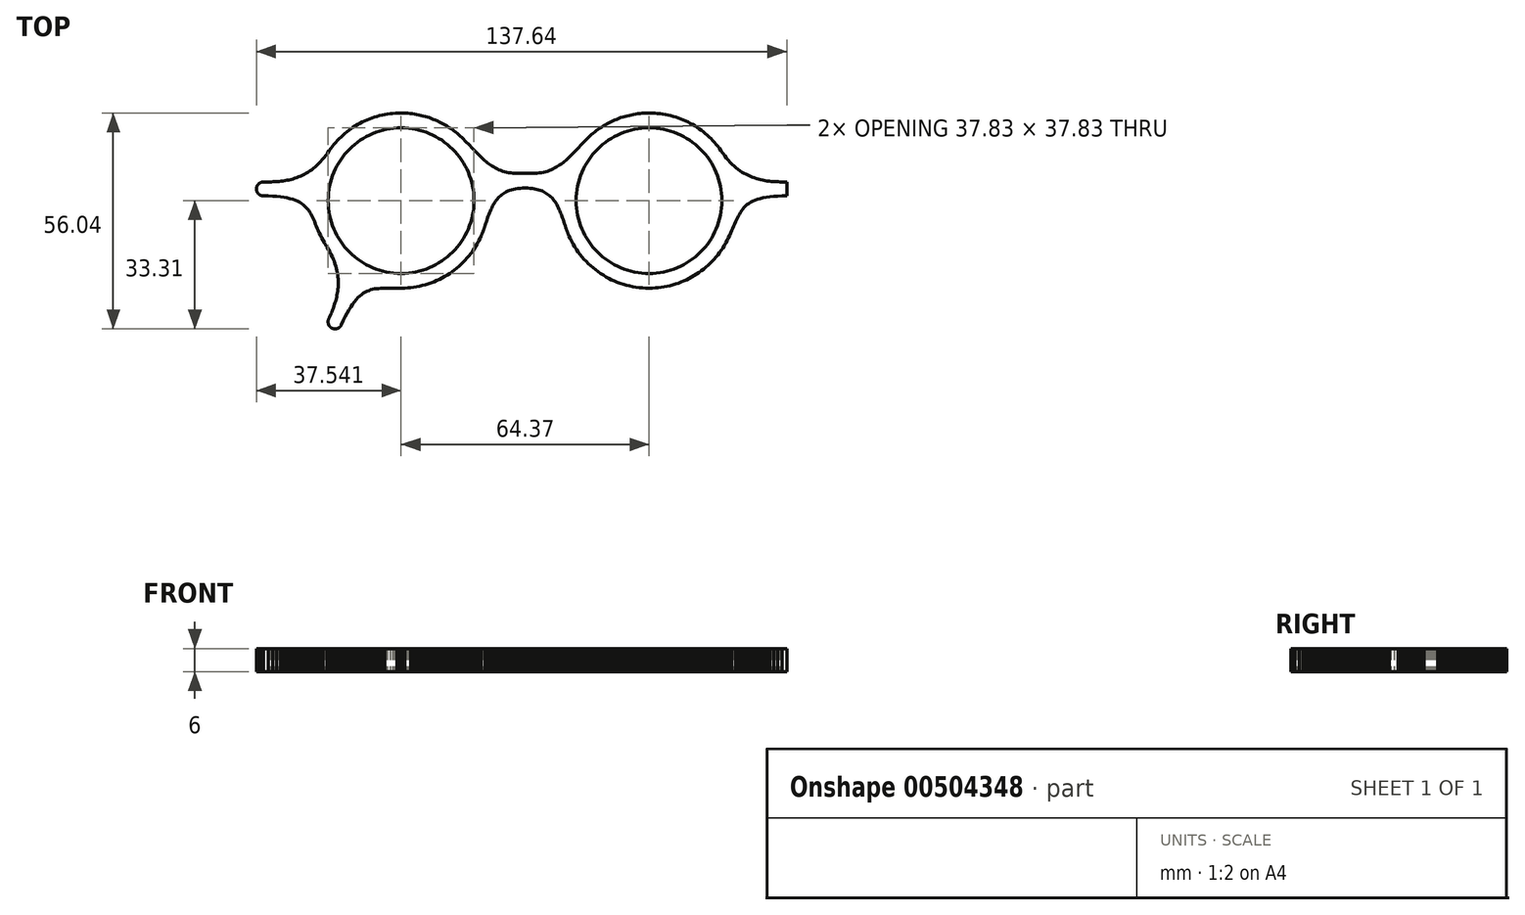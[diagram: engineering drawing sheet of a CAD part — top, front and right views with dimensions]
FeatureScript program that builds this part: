
annotation { "Feature Type Name" : "Feature", "Feature Type Description" : "" }
export const myFeature = defineFeature(function(context is Context, id is Id, definition is map)
    precondition{}
    {
        {
            var Q0;
            Q0=qCreatedBy(makeId("Top.planeOp"),FACE);
            var sketch = newSketch(context, id + "F0", { "sketchPlane" : qUnion([Q0])});
            skLineSegment(sketch, "E0", {"start": v(51.75, 18.26) * mm, "end": v(51.75, 18.26) * mm});
            skLineSegment(sketch, "E1", {"start": v(51.75, 18.26) * mm, "end": v(51.74, 18.27) * mm});
            skLineSegment(sketch, "E2", {"start": v(51.74, 18.27) * mm, "end": v(51.74, 18.27) * mm});
            skLineSegment(sketch, "E3", {"start": v(51.74, 18.27) * mm, "end": v(51.74, 18.28) * mm});
            skLineSegment(sketch, "E4", {"start": v(51.74, 18.28) * mm, "end": v(51.74, 18.28) * mm});
            skLineSegment(sketch, "E5", {"start": v(51.74, 18.28) * mm, "end": v(51.73, 18.28) * mm});
            skLineSegment(sketch, "E6", {"start": v(51.73, 18.28) * mm, "end": v(51.73, 18.28) * mm});
            skLineSegment(sketch, "E7", {"start": v(51.73, 18.28) * mm, "end": v(51.73, 18.29) * mm});
            skLineSegment(sketch, "E8", {"start": v(51.73, 18.29) * mm, "end": v(51.73, 18.29) * mm});
            skLineSegment(sketch, "E9", {"start": v(51.73, 18.29) * mm, "end": v(51.73, 18.28) * mm});
            skLineSegment(sketch, "E10", {"start": v(51.73, 18.28) * mm, "end": v(51.74, 18.28) * mm});
            skLineSegment(sketch, "E11", {"start": v(51.74, 18.28) * mm, "end": v(51.74, 18.27) * mm});
            skLineSegment(sketch, "E12", {"start": v(51.74, 18.27) * mm, "end": v(51.74, 18.26) * mm});
            skLineSegment(sketch, "E13", {"start": v(51.74, 18.26) * mm, "end": v(51.75, 18.26) * mm});
            skLineSegment(sketch, "E14", {"start": v(-49.93, 18.27) * mm, "end": v(-49.93, 18.27) * mm});
            skLineSegment(sketch, "E15", {"start": v(-49.93, 18.27) * mm, "end": v(-49.92, 18.28) * mm});
            skLineSegment(sketch, "E16", {"start": v(-49.92, 18.28) * mm, "end": v(-49.92, 18.28) * mm});
            skLineSegment(sketch, "E17", {"start": v(-49.92, 18.28) * mm, "end": v(-49.92, 18.29) * mm});
            skLineSegment(sketch, "E18", {"start": v(-49.92, 18.29) * mm, "end": v(-49.92, 18.29) * mm});
            skLineSegment(sketch, "E19", {"start": v(-49.92, 18.29) * mm, "end": v(-49.92, 18.28) * mm});
            skLineSegment(sketch, "E20", {"start": v(-49.92, 18.28) * mm, "end": v(-49.93, 18.27) * mm});
            skLineSegment(sketch, "E21", {"start": v(-49.93, 18.27) * mm, "end": v(-49.93, 18.26) * mm});
            skLineSegment(sketch, "E22", {"start": v(-49.93, 18.26) * mm, "end": v(-49.93, 18.26) * mm});
            skLineSegment(sketch, "E23", {"start": v(-49.93, 18.26) * mm, "end": v(-49.94, 18.26) * mm});
            skLineSegment(sketch, "E24", {"start": v(-49.94, 18.26) * mm, "end": v(-49.94, 18.26) * mm});
            skLineSegment(sketch, "E25", {"start": v(-49.94, 18.26) * mm, "end": v(-49.93, 18.26) * mm});
            skLineSegment(sketch, "E26", {"start": v(-49.93, 18.26) * mm, "end": v(-49.93, 18.27) * mm});
            skLineSegment(sketch, "E27", {"start": v(68.25, 10.13) * mm, "end": v(67.67, 10.14) * mm});
            skLineSegment(sketch, "E28", {"start": v(67.67, 10.14) * mm, "end": v(67.1, 10.15) * mm});
            skLineSegment(sketch, "E29", {"start": v(67.1, 10.15) * mm, "end": v(66.53, 10.17) * mm});
            skLineSegment(sketch, "E30", {"start": v(66.53, 10.17) * mm, "end": v(65.97, 10.2) * mm});
            skLineSegment(sketch, "E31", {"start": v(65.97, 10.2) * mm, "end": v(65.4, 10.23) * mm});
            skLineSegment(sketch, "E32", {"start": v(65.4, 10.23) * mm, "end": v(64.84, 10.28) * mm});
            skLineSegment(sketch, "E33", {"start": v(64.84, 10.28) * mm, "end": v(64.27, 10.34) * mm});
            skLineSegment(sketch, "E34", {"start": v(64.27, 10.34) * mm, "end": v(63.72, 10.41) * mm});
            skLineSegment(sketch, "E35", {"start": v(63.72, 10.41) * mm, "end": v(63.16, 10.5) * mm});
            skLineSegment(sketch, "E36", {"start": v(63.16, 10.5) * mm, "end": v(62.6, 10.6) * mm});
            skLineSegment(sketch, "E37", {"start": v(62.6, 10.6) * mm, "end": v(62.05, 10.72) * mm});
            skLineSegment(sketch, "E38", {"start": v(62.05, 10.72) * mm, "end": v(61.5, 10.85) * mm});
            skLineSegment(sketch, "E39", {"start": v(61.5, 10.85) * mm, "end": v(60.96, 11) * mm});
            skLineSegment(sketch, "E40", {"start": v(60.96, 11) * mm, "end": v(60.42, 11.18) * mm});
            skLineSegment(sketch, "E41", {"start": v(60.42, 11.18) * mm, "end": v(59.88, 11.38) * mm});
            skLineSegment(sketch, "E42", {"start": v(59.88, 11.38) * mm, "end": v(59.34, 11.6) * mm});
            skLineSegment(sketch, "E43", {"start": v(59.34, 11.6) * mm, "end": v(58.8, 11.83) * mm});
            skLineSegment(sketch, "E44", {"start": v(58.8, 11.83) * mm, "end": v(58.28, 12.1) * mm});
            skLineSegment(sketch, "E45", {"start": v(58.28, 12.1) * mm, "end": v(57.75, 12.38) * mm});
            skLineSegment(sketch, "E46", {"start": v(57.75, 12.38) * mm, "end": v(57.23, 12.7) * mm});
            skLineSegment(sketch, "E47", {"start": v(57.23, 12.7) * mm, "end": v(56.71, 13.04) * mm});
            skLineSegment(sketch, "E48", {"start": v(56.71, 13.04) * mm, "end": v(56.2, 13.42) * mm});
            skLineSegment(sketch, "E49", {"start": v(56.2, 13.42) * mm, "end": v(55.69, 13.82) * mm});
            skLineSegment(sketch, "E50", {"start": v(55.69, 13.82) * mm, "end": v(55.18, 14.25) * mm});
            skLineSegment(sketch, "E51", {"start": v(55.18, 14.25) * mm, "end": v(54.68, 14.72) * mm});
            skLineSegment(sketch, "E52", {"start": v(54.68, 14.72) * mm, "end": v(54.18, 15.22) * mm});
            skLineSegment(sketch, "E53", {"start": v(54.18, 15.22) * mm, "end": v(53.68, 15.75) * mm});
            skLineSegment(sketch, "E54", {"start": v(53.68, 15.75) * mm, "end": v(53.2, 16.32) * mm});
            skLineSegment(sketch, "E55", {"start": v(53.2, 16.32) * mm, "end": v(52.7, 16.93) * mm});
            skLineSegment(sketch, "E56", {"start": v(52.7, 16.93) * mm, "end": v(52.22, 17.57) * mm});
            skLineSegment(sketch, "E57", {"start": v(52.22, 17.57) * mm, "end": v(51.75, 18.26) * mm});
            skLineSegment(sketch, "E58", {"start": v(51.75, 18.26) * mm, "end": v(51.35, 18.8) * mm});
            skLineSegment(sketch, "E59", {"start": v(51.35, 18.8) * mm, "end": v(50.95, 19.34) * mm});
            skLineSegment(sketch, "E60", {"start": v(50.95, 19.34) * mm, "end": v(50.52, 19.86) * mm});
            skLineSegment(sketch, "E61", {"start": v(50.52, 19.86) * mm, "end": v(50.08, 20.37) * mm});
            skLineSegment(sketch, "E62", {"start": v(50.08, 20.37) * mm, "end": v(49.63, 20.87) * mm});
            skLineSegment(sketch, "E63", {"start": v(49.63, 20.87) * mm, "end": v(49.16, 21.35) * mm});
            skLineSegment(sketch, "E64", {"start": v(49.16, 21.35) * mm, "end": v(48.68, 21.82) * mm});
            skLineSegment(sketch, "E65", {"start": v(48.68, 21.82) * mm, "end": v(48.18, 22.27) * mm});
            skLineSegment(sketch, "E66", {"start": v(48.18, 22.27) * mm, "end": v(47.68, 22.71) * mm});
            skLineSegment(sketch, "E67", {"start": v(47.68, 22.71) * mm, "end": v(47.15, 23.14) * mm});
            skLineSegment(sketch, "E68", {"start": v(47.15, 23.14) * mm, "end": v(46.62, 23.55) * mm});
            skLineSegment(sketch, "E69", {"start": v(46.62, 23.55) * mm, "end": v(46.07, 23.94) * mm});
            skLineSegment(sketch, "E70", {"start": v(46.07, 23.94) * mm, "end": v(45.51, 24.32) * mm});
            skLineSegment(sketch, "E71", {"start": v(45.51, 24.32) * mm, "end": v(44.94, 24.68) * mm});
            skLineSegment(sketch, "E72", {"start": v(44.94, 24.68) * mm, "end": v(44.36, 25.02) * mm});
            skLineSegment(sketch, "E73", {"start": v(44.36, 25.02) * mm, "end": v(43.77, 25.35) * mm});
            skLineSegment(sketch, "E74", {"start": v(43.77, 25.35) * mm, "end": v(43.17, 25.66) * mm});
            skLineSegment(sketch, "E75", {"start": v(43.17, 25.66) * mm, "end": v(42.56, 25.96) * mm});
            skLineSegment(sketch, "E76", {"start": v(42.56, 25.96) * mm, "end": v(41.93, 26.23) * mm});
            skLineSegment(sketch, "E77", {"start": v(41.93, 26.23) * mm, "end": v(41.3, 26.49) * mm});
            skLineSegment(sketch, "E78", {"start": v(41.3, 26.49) * mm, "end": v(40.66, 26.73) * mm});
            skLineSegment(sketch, "E79", {"start": v(40.66, 26.73) * mm, "end": v(40.01, 26.95) * mm});
            skLineSegment(sketch, "E80", {"start": v(40.01, 26.95) * mm, "end": v(39.35, 27.15) * mm});
            skLineSegment(sketch, "E81", {"start": v(39.35, 27.15) * mm, "end": v(38.68, 27.33) * mm});
            skLineSegment(sketch, "E82", {"start": v(38.68, 27.33) * mm, "end": v(38, 27.49) * mm});
            skLineSegment(sketch, "E83", {"start": v(38, 27.49) * mm, "end": v(37.33, 27.63) * mm});
            skLineSegment(sketch, "E84", {"start": v(37.33, 27.63) * mm, "end": v(36.64, 27.75) * mm});
            skLineSegment(sketch, "E85", {"start": v(36.64, 27.75) * mm, "end": v(35.94, 27.85) * mm});
            skLineSegment(sketch, "E86", {"start": v(35.94, 27.85) * mm, "end": v(35.24, 27.92) * mm});
            skLineSegment(sketch, "E87", {"start": v(35.24, 27.92) * mm, "end": v(34.53, 27.98) * mm});
            skLineSegment(sketch, "E88", {"start": v(34.53, 27.98) * mm, "end": v(33.81, 28.01) * mm});
            skLineSegment(sketch, "E89", {"start": v(33.81, 28.01) * mm, "end": v(33.1, 28.02) * mm});
            skLineSegment(sketch, "E90", {"start": v(33.1, 28.02) * mm, "end": v(32.5, 28.02) * mm});
            skLineSegment(sketch, "E91", {"start": v(32.5, 28.02) * mm, "end": v(31.91, 28) * mm});
            skLineSegment(sketch, "E92", {"start": v(31.91, 28) * mm, "end": v(31.33, 27.96) * mm});
            skLineSegment(sketch, "E93", {"start": v(31.33, 27.96) * mm, "end": v(30.75, 27.9) * mm});
            skLineSegment(sketch, "E94", {"start": v(30.75, 27.9) * mm, "end": v(30.18, 27.84) * mm});
            skLineSegment(sketch, "E95", {"start": v(30.18, 27.84) * mm, "end": v(29.6, 27.76) * mm});
            skLineSegment(sketch, "E96", {"start": v(29.6, 27.76) * mm, "end": v(29.04, 27.66) * mm});
            skLineSegment(sketch, "E97", {"start": v(29.04, 27.66) * mm, "end": v(28.48, 27.55) * mm});
            skLineSegment(sketch, "E98", {"start": v(28.48, 27.55) * mm, "end": v(27.92, 27.43) * mm});
            skLineSegment(sketch, "E99", {"start": v(27.92, 27.43) * mm, "end": v(27.37, 27.3) * mm});
            skLineSegment(sketch, "E100", {"start": v(27.37, 27.3) * mm, "end": v(26.82, 27.14) * mm});
            skLineSegment(sketch, "E101", {"start": v(26.82, 27.14) * mm, "end": v(26.28, 26.98) * mm});
            skLineSegment(sketch, "E102", {"start": v(26.28, 26.98) * mm, "end": v(25.75, 26.8) * mm});
            skLineSegment(sketch, "E103", {"start": v(25.75, 26.8) * mm, "end": v(25.22, 26.62) * mm});
            skLineSegment(sketch, "E104", {"start": v(25.22, 26.62) * mm, "end": v(24.7, 26.42) * mm});
            skLineSegment(sketch, "E105", {"start": v(24.7, 26.42) * mm, "end": v(24.18, 26.2) * mm});
            skLineSegment(sketch, "E106", {"start": v(24.18, 26.2) * mm, "end": v(23.67, 25.98) * mm});
            skLineSegment(sketch, "E107", {"start": v(23.67, 25.98) * mm, "end": v(23.17, 25.74) * mm});
            skLineSegment(sketch, "E108", {"start": v(23.17, 25.74) * mm, "end": v(22.67, 25.5) * mm});
            skLineSegment(sketch, "E109", {"start": v(22.67, 25.5) * mm, "end": v(22.18, 25.23) * mm});
            skLineSegment(sketch, "E110", {"start": v(22.18, 25.23) * mm, "end": v(21.7, 24.96) * mm});
            skLineSegment(sketch, "E111", {"start": v(21.7, 24.96) * mm, "end": v(21.22, 24.67) * mm});
            skLineSegment(sketch, "E112", {"start": v(21.22, 24.67) * mm, "end": v(20.76, 24.38) * mm});
            skLineSegment(sketch, "E113", {"start": v(20.76, 24.38) * mm, "end": v(20.3, 24.07) * mm});
            skLineSegment(sketch, "E114", {"start": v(20.3, 24.07) * mm, "end": v(19.84, 23.75) * mm});
            skLineSegment(sketch, "E115", {"start": v(19.84, 23.75) * mm, "end": v(19.4, 23.43) * mm});
            skLineSegment(sketch, "E116", {"start": v(19.4, 23.43) * mm, "end": v(18.97, 23.09) * mm});
            skLineSegment(sketch, "E117", {"start": v(18.97, 23.09) * mm, "end": v(18.54, 22.74) * mm});
            skLineSegment(sketch, "E118", {"start": v(18.54, 22.74) * mm, "end": v(18.12, 22.38) * mm});
            skLineSegment(sketch, "E119", {"start": v(18.12, 22.38) * mm, "end": v(17.71, 22.01) * mm});
            skLineSegment(sketch, "E120", {"start": v(17.71, 22.01) * mm, "end": v(17.31, 21.64) * mm});
            skLineSegment(sketch, "E121", {"start": v(17.31, 21.64) * mm, "end": v(16.92, 21.25) * mm});
            skLineSegment(sketch, "E122", {"start": v(16.92, 21.25) * mm, "end": v(16.49, 20.82) * mm});
            skLineSegment(sketch, "E123", {"start": v(16.49, 20.82) * mm, "end": v(16.07, 20.4) * mm});
            skLineSegment(sketch, "E124", {"start": v(16.07, 20.4) * mm, "end": v(15.66, 19.98) * mm});
            skLineSegment(sketch, "E125", {"start": v(15.66, 19.98) * mm, "end": v(15.26, 19.56) * mm});
            skLineSegment(sketch, "E126", {"start": v(15.26, 19.56) * mm, "end": v(14.86, 19.15) * mm});
            skLineSegment(sketch, "E127", {"start": v(14.86, 19.15) * mm, "end": v(14.47, 18.74) * mm});
            skLineSegment(sketch, "E128", {"start": v(14.47, 18.74) * mm, "end": v(14.09, 18.34) * mm});
            skLineSegment(sketch, "E129", {"start": v(14.09, 18.34) * mm, "end": v(13.71, 17.95) * mm});
            skLineSegment(sketch, "E130", {"start": v(13.71, 17.95) * mm, "end": v(13.33, 17.56) * mm});
            skLineSegment(sketch, "E131", {"start": v(13.33, 17.56) * mm, "end": v(12.96, 17.18) * mm});
            skLineSegment(sketch, "E132", {"start": v(12.96, 17.18) * mm, "end": v(12.58, 16.8) * mm});
            skLineSegment(sketch, "E133", {"start": v(12.58, 16.8) * mm, "end": v(12.2, 16.44) * mm});
            skLineSegment(sketch, "E134", {"start": v(12.2, 16.44) * mm, "end": v(11.83, 16.1) * mm});
            skLineSegment(sketch, "E135", {"start": v(11.83, 16.1) * mm, "end": v(11.45, 15.75) * mm});
            skLineSegment(sketch, "E136", {"start": v(11.45, 15.75) * mm, "end": v(11.06, 15.42) * mm});
            skLineSegment(sketch, "E137", {"start": v(11.06, 15.42) * mm, "end": v(10.67, 15.1) * mm});
            skLineSegment(sketch, "E138", {"start": v(10.67, 15.1) * mm, "end": v(10.28, 14.8) * mm});
            skLineSegment(sketch, "E139", {"start": v(10.28, 14.8) * mm, "end": v(9.87, 14.5) * mm});
            skLineSegment(sketch, "E140", {"start": v(9.87, 14.5) * mm, "end": v(9.46, 14.23) * mm});
            skLineSegment(sketch, "E141", {"start": v(9.46, 14.23) * mm, "end": v(9.04, 13.98) * mm});
            skLineSegment(sketch, "E142", {"start": v(9.04, 13.98) * mm, "end": v(8.6, 13.73) * mm});
            skLineSegment(sketch, "E143", {"start": v(8.6, 13.73) * mm, "end": v(8.16, 13.5) * mm});
            skLineSegment(sketch, "E144", {"start": v(8.16, 13.5) * mm, "end": v(7.7, 13.3) * mm});
            skLineSegment(sketch, "E145", {"start": v(7.7, 13.3) * mm, "end": v(7.23, 13.1) * mm});
            skLineSegment(sketch, "E146", {"start": v(7.23, 13.1) * mm, "end": v(6.74, 12.94) * mm});
            skLineSegment(sketch, "E147", {"start": v(6.74, 12.94) * mm, "end": v(6.24, 12.79) * mm});
            skLineSegment(sketch, "E148", {"start": v(6.24, 12.79) * mm, "end": v(5.72, 12.66) * mm});
            skLineSegment(sketch, "E149", {"start": v(5.72, 12.66) * mm, "end": v(5.18, 12.55) * mm});
            skLineSegment(sketch, "E150", {"start": v(5.18, 12.55) * mm, "end": v(4.62, 12.47) * mm});
            skLineSegment(sketch, "E151", {"start": v(4.62, 12.47) * mm, "end": v(4.03, 12.4) * mm});
            skLineSegment(sketch, "E152", {"start": v(4.03, 12.4) * mm, "end": v(3.43, 12.37) * mm});
            skLineSegment(sketch, "E153", {"start": v(3.43, 12.37) * mm, "end": v(2.8, 12.36) * mm});
            skLineSegment(sketch, "E154", {"start": v(2.8, 12.36) * mm, "end": v(2.69, 12.36) * mm});
            skLineSegment(sketch, "E155", {"start": v(2.69, 12.36) * mm, "end": v(2.57, 12.36) * mm});
            skLineSegment(sketch, "E156", {"start": v(2.57, 12.36) * mm, "end": v(2.45, 12.36) * mm});
            skLineSegment(sketch, "E157", {"start": v(2.45, 12.36) * mm, "end": v(2.33, 12.36) * mm});
            skLineSegment(sketch, "E158", {"start": v(2.33, 12.36) * mm, "end": v(2.21, 12.36) * mm});
            skLineSegment(sketch, "E159", {"start": v(2.21, 12.36) * mm, "end": v(2.1, 12.36) * mm});
            skLineSegment(sketch, "E160", {"start": v(2.1, 12.36) * mm, "end": v(1.97, 12.36) * mm});
            skLineSegment(sketch, "E161", {"start": v(1.97, 12.36) * mm, "end": v(1.86, 12.36) * mm});
            skLineSegment(sketch, "E162", {"start": v(1.86, 12.36) * mm, "end": v(1.74, 12.36) * mm});
            skLineSegment(sketch, "E163", {"start": v(1.74, 12.36) * mm, "end": v(1.62, 12.36) * mm});
            skLineSegment(sketch, "E164", {"start": v(1.62, 12.36) * mm, "end": v(1.5, 12.36) * mm});
            skLineSegment(sketch, "E165", {"start": v(1.5, 12.36) * mm, "end": v(1.38, 12.36) * mm});
            skLineSegment(sketch, "E166", {"start": v(1.38, 12.36) * mm, "end": v(1.26, 12.36) * mm});
            skLineSegment(sketch, "E167", {"start": v(1.26, 12.36) * mm, "end": v(1.14, 12.36) * mm});
            skLineSegment(sketch, "E168", {"start": v(1.14, 12.36) * mm, "end": v(1.02, 12.36) * mm});
            skLineSegment(sketch, "E169", {"start": v(1.02, 12.36) * mm, "end": v(0.9, 12.36) * mm});
            skLineSegment(sketch, "E170", {"start": v(0.9, 12.36) * mm, "end": v(0.79, 12.36) * mm});
            skLineSegment(sketch, "E171", {"start": v(0.79, 12.36) * mm, "end": v(0.67, 12.36) * mm});
            skLineSegment(sketch, "E172", {"start": v(0.67, 12.36) * mm, "end": v(0.55, 12.36) * mm});
            skLineSegment(sketch, "E173", {"start": v(0.55, 12.36) * mm, "end": v(0.43, 12.36) * mm});
            skLineSegment(sketch, "E174", {"start": v(0.43, 12.36) * mm, "end": v(0.31, 12.36) * mm});
            skLineSegment(sketch, "E175", {"start": v(0.31, 12.36) * mm, "end": v(0.2, 12.36) * mm});
            skLineSegment(sketch, "E176", {"start": v(0.2, 12.36) * mm, "end": v(0.08, 12.36) * mm});
            skLineSegment(sketch, "E177", {"start": v(0.08, 12.36) * mm, "end": v(-0.04, 12.36) * mm});
            skLineSegment(sketch, "E178", {"start": v(-0.04, 12.36) * mm, "end": v(-0.16, 12.36) * mm});
            skLineSegment(sketch, "E179", {"start": v(-0.16, 12.36) * mm, "end": v(-0.28, 12.36) * mm});
            skLineSegment(sketch, "E180", {"start": v(-0.28, 12.36) * mm, "end": v(-0.4, 12.36) * mm});
            skLineSegment(sketch, "E181", {"start": v(-0.4, 12.36) * mm, "end": v(-0.52, 12.36) * mm});
            skLineSegment(sketch, "E182", {"start": v(-0.52, 12.36) * mm, "end": v(-0.64, 12.36) * mm});
            skLineSegment(sketch, "E183", {"start": v(-0.64, 12.36) * mm, "end": v(-0.75, 12.36) * mm});
            skLineSegment(sketch, "E184", {"start": v(-0.75, 12.36) * mm, "end": v(-0.87, 12.36) * mm});
            skLineSegment(sketch, "E185", {"start": v(-0.87, 12.36) * mm, "end": v(-1, 12.36) * mm});
            skLineSegment(sketch, "E186", {"start": v(-1, 12.36) * mm, "end": v(-1.62, 12.37) * mm});
            skLineSegment(sketch, "E187", {"start": v(-1.62, 12.37) * mm, "end": v(-2.22, 12.4) * mm});
            skLineSegment(sketch, "E188", {"start": v(-2.22, 12.4) * mm, "end": v(-2.8, 12.47) * mm});
            skLineSegment(sketch, "E189", {"start": v(-2.8, 12.47) * mm, "end": v(-3.36, 12.55) * mm});
            skLineSegment(sketch, "E190", {"start": v(-3.36, 12.55) * mm, "end": v(-3.9, 12.66) * mm});
            skLineSegment(sketch, "E191", {"start": v(-3.9, 12.66) * mm, "end": v(-4.43, 12.79) * mm});
            skLineSegment(sketch, "E192", {"start": v(-4.43, 12.79) * mm, "end": v(-4.93, 12.94) * mm});
            skLineSegment(sketch, "E193", {"start": v(-4.93, 12.94) * mm, "end": v(-5.42, 13.1) * mm});
            skLineSegment(sketch, "E194", {"start": v(-5.42, 13.1) * mm, "end": v(-5.9, 13.3) * mm});
            skLineSegment(sketch, "E195", {"start": v(-5.9, 13.3) * mm, "end": v(-6.35, 13.5) * mm});
            skLineSegment(sketch, "E196", {"start": v(-6.35, 13.5) * mm, "end": v(-6.8, 13.73) * mm});
            skLineSegment(sketch, "E197", {"start": v(-6.8, 13.73) * mm, "end": v(-7.23, 13.98) * mm});
            skLineSegment(sketch, "E198", {"start": v(-7.23, 13.98) * mm, "end": v(-7.65, 14.23) * mm});
            skLineSegment(sketch, "E199", {"start": v(-7.65, 14.23) * mm, "end": v(-8.06, 14.5) * mm});
            skLineSegment(sketch, "E200", {"start": v(-8.06, 14.5) * mm, "end": v(-8.46, 14.8) * mm});
            skLineSegment(sketch, "E201", {"start": v(-8.46, 14.8) * mm, "end": v(-8.86, 15.1) * mm});
            skLineSegment(sketch, "E202", {"start": v(-8.86, 15.1) * mm, "end": v(-9.25, 15.42) * mm});
            skLineSegment(sketch, "E203", {"start": v(-9.25, 15.42) * mm, "end": v(-9.64, 15.75) * mm});
            skLineSegment(sketch, "E204", {"start": v(-9.64, 15.75) * mm, "end": v(-10.02, 16.1) * mm});
            skLineSegment(sketch, "E205", {"start": v(-10.02, 16.1) * mm, "end": v(-10.4, 16.44) * mm});
            skLineSegment(sketch, "E206", {"start": v(-10.4, 16.44) * mm, "end": v(-10.77, 16.8) * mm});
            skLineSegment(sketch, "E207", {"start": v(-10.77, 16.8) * mm, "end": v(-11.15, 17.18) * mm});
            skLineSegment(sketch, "E208", {"start": v(-11.15, 17.18) * mm, "end": v(-11.52, 17.56) * mm});
            skLineSegment(sketch, "E209", {"start": v(-11.52, 17.56) * mm, "end": v(-11.9, 17.95) * mm});
            skLineSegment(sketch, "E210", {"start": v(-11.9, 17.95) * mm, "end": v(-12.28, 18.34) * mm});
            skLineSegment(sketch, "E211", {"start": v(-12.28, 18.34) * mm, "end": v(-12.66, 18.74) * mm});
            skLineSegment(sketch, "E212", {"start": v(-12.66, 18.74) * mm, "end": v(-13.05, 19.15) * mm});
            skLineSegment(sketch, "E213", {"start": v(-13.05, 19.15) * mm, "end": v(-13.45, 19.56) * mm});
            skLineSegment(sketch, "E214", {"start": v(-13.45, 19.56) * mm, "end": v(-13.85, 19.98) * mm});
            skLineSegment(sketch, "E215", {"start": v(-13.85, 19.98) * mm, "end": v(-14.26, 20.4) * mm});
            skLineSegment(sketch, "E216", {"start": v(-14.26, 20.4) * mm, "end": v(-14.68, 20.82) * mm});
            skLineSegment(sketch, "E217", {"start": v(-14.68, 20.82) * mm, "end": v(-15.1, 21.25) * mm});
            skLineSegment(sketch, "E218", {"start": v(-15.1, 21.25) * mm, "end": v(-15.5, 21.64) * mm});
            skLineSegment(sketch, "E219", {"start": v(-15.5, 21.64) * mm, "end": v(-15.9, 22.01) * mm});
            skLineSegment(sketch, "E220", {"start": v(-15.9, 22.01) * mm, "end": v(-16.3, 22.38) * mm});
            skLineSegment(sketch, "E221", {"start": v(-16.3, 22.38) * mm, "end": v(-16.73, 22.74) * mm});
            skLineSegment(sketch, "E222", {"start": v(-16.73, 22.74) * mm, "end": v(-17.15, 23.09) * mm});
            skLineSegment(sketch, "E223", {"start": v(-17.15, 23.09) * mm, "end": v(-17.59, 23.43) * mm});
            skLineSegment(sketch, "E224", {"start": v(-17.59, 23.43) * mm, "end": v(-18.03, 23.75) * mm});
            skLineSegment(sketch, "E225", {"start": v(-18.03, 23.75) * mm, "end": v(-18.48, 24.07) * mm});
            skLineSegment(sketch, "E226", {"start": v(-18.48, 24.07) * mm, "end": v(-18.94, 24.38) * mm});
            skLineSegment(sketch, "E227", {"start": v(-18.94, 24.38) * mm, "end": v(-19.41, 24.67) * mm});
            skLineSegment(sketch, "E228", {"start": v(-19.41, 24.67) * mm, "end": v(-19.89, 24.96) * mm});
            skLineSegment(sketch, "E229", {"start": v(-19.89, 24.96) * mm, "end": v(-20.37, 25.23) * mm});
            skLineSegment(sketch, "E230", {"start": v(-20.37, 25.23) * mm, "end": v(-20.86, 25.5) * mm});
            skLineSegment(sketch, "E231", {"start": v(-20.86, 25.5) * mm, "end": v(-21.36, 25.74) * mm});
            skLineSegment(sketch, "E232", {"start": v(-21.36, 25.74) * mm, "end": v(-21.86, 25.98) * mm});
            skLineSegment(sketch, "E233", {"start": v(-21.86, 25.98) * mm, "end": v(-22.37, 26.2) * mm});
            skLineSegment(sketch, "E234", {"start": v(-22.37, 26.2) * mm, "end": v(-22.89, 26.42) * mm});
            skLineSegment(sketch, "E235", {"start": v(-22.89, 26.42) * mm, "end": v(-23.4, 26.62) * mm});
            skLineSegment(sketch, "E236", {"start": v(-23.4, 26.62) * mm, "end": v(-23.94, 26.8) * mm});
            skLineSegment(sketch, "E237", {"start": v(-23.94, 26.8) * mm, "end": v(-24.47, 26.98) * mm});
            skLineSegment(sketch, "E238", {"start": v(-24.47, 26.98) * mm, "end": v(-25.01, 27.14) * mm});
            skLineSegment(sketch, "E239", {"start": v(-25.01, 27.14) * mm, "end": v(-25.56, 27.3) * mm});
            skLineSegment(sketch, "E240", {"start": v(-25.56, 27.3) * mm, "end": v(-26.1, 27.43) * mm});
            skLineSegment(sketch, "E241", {"start": v(-26.1, 27.43) * mm, "end": v(-26.67, 27.55) * mm});
            skLineSegment(sketch, "E242", {"start": v(-26.67, 27.55) * mm, "end": v(-27.23, 27.66) * mm});
            skLineSegment(sketch, "E243", {"start": v(-27.23, 27.66) * mm, "end": v(-27.8, 27.76) * mm});
            skLineSegment(sketch, "E244", {"start": v(-27.8, 27.76) * mm, "end": v(-28.36, 27.84) * mm});
            skLineSegment(sketch, "E245", {"start": v(-28.36, 27.84) * mm, "end": v(-28.94, 27.9) * mm});
            skLineSegment(sketch, "E246", {"start": v(-28.94, 27.9) * mm, "end": v(-29.52, 27.96) * mm});
            skLineSegment(sketch, "E247", {"start": v(-29.52, 27.96) * mm, "end": v(-30.1, 28) * mm});
            skLineSegment(sketch, "E248", {"start": v(-30.1, 28) * mm, "end": v(-30.69, 28.02) * mm});
            skLineSegment(sketch, "E249", {"start": v(-30.69, 28.02) * mm, "end": v(-31.28, 28.02) * mm});
            skLineSegment(sketch, "E250", {"start": v(-31.28, 28.02) * mm, "end": v(-32, 28.01) * mm});
            skLineSegment(sketch, "E251", {"start": v(-32, 28.01) * mm, "end": v(-32.72, 27.98) * mm});
            skLineSegment(sketch, "E252", {"start": v(-32.72, 27.98) * mm, "end": v(-33.42, 27.92) * mm});
            skLineSegment(sketch, "E253", {"start": v(-33.42, 27.92) * mm, "end": v(-34.13, 27.85) * mm});
            skLineSegment(sketch, "E254", {"start": v(-34.13, 27.85) * mm, "end": v(-34.82, 27.75) * mm});
            skLineSegment(sketch, "E255", {"start": v(-34.82, 27.75) * mm, "end": v(-35.51, 27.63) * mm});
            skLineSegment(sketch, "E256", {"start": v(-35.51, 27.63) * mm, "end": v(-36.2, 27.49) * mm});
            skLineSegment(sketch, "E257", {"start": v(-36.2, 27.49) * mm, "end": v(-36.87, 27.33) * mm});
            skLineSegment(sketch, "E258", {"start": v(-36.87, 27.33) * mm, "end": v(-37.54, 27.15) * mm});
            skLineSegment(sketch, "E259", {"start": v(-37.54, 27.15) * mm, "end": v(-38.2, 26.95) * mm});
            skLineSegment(sketch, "E260", {"start": v(-38.2, 26.95) * mm, "end": v(-38.85, 26.73) * mm});
            skLineSegment(sketch, "E261", {"start": v(-38.85, 26.73) * mm, "end": v(-39.49, 26.49) * mm});
            skLineSegment(sketch, "E262", {"start": v(-39.49, 26.49) * mm, "end": v(-40.12, 26.23) * mm});
            skLineSegment(sketch, "E263", {"start": v(-40.12, 26.23) * mm, "end": v(-40.74, 25.96) * mm});
            skLineSegment(sketch, "E264", {"start": v(-40.74, 25.96) * mm, "end": v(-41.36, 25.66) * mm});
            skLineSegment(sketch, "E265", {"start": v(-41.36, 25.66) * mm, "end": v(-41.96, 25.35) * mm});
            skLineSegment(sketch, "E266", {"start": v(-41.96, 25.35) * mm, "end": v(-42.55, 25.02) * mm});
            skLineSegment(sketch, "E267", {"start": v(-42.55, 25.02) * mm, "end": v(-43.13, 24.68) * mm});
            skLineSegment(sketch, "E268", {"start": v(-43.13, 24.68) * mm, "end": v(-43.7, 24.32) * mm});
            skLineSegment(sketch, "E269", {"start": v(-43.7, 24.32) * mm, "end": v(-44.26, 23.94) * mm});
            skLineSegment(sketch, "E270", {"start": v(-44.26, 23.94) * mm, "end": v(-44.8, 23.55) * mm});
            skLineSegment(sketch, "E271", {"start": v(-44.8, 23.55) * mm, "end": v(-45.34, 23.14) * mm});
            skLineSegment(sketch, "E272", {"start": v(-45.34, 23.14) * mm, "end": v(-45.86, 22.71) * mm});
            skLineSegment(sketch, "E273", {"start": v(-45.86, 22.71) * mm, "end": v(-46.37, 22.27) * mm});
            skLineSegment(sketch, "E274", {"start": v(-46.37, 22.27) * mm, "end": v(-46.87, 21.82) * mm});
            skLineSegment(sketch, "E275", {"start": v(-46.87, 21.82) * mm, "end": v(-47.35, 21.35) * mm});
            skLineSegment(sketch, "E276", {"start": v(-47.35, 21.35) * mm, "end": v(-47.82, 20.87) * mm});
            skLineSegment(sketch, "E277", {"start": v(-47.82, 20.87) * mm, "end": v(-48.27, 20.37) * mm});
            skLineSegment(sketch, "E278", {"start": v(-48.27, 20.37) * mm, "end": v(-48.7, 19.86) * mm});
            skLineSegment(sketch, "E279", {"start": v(-48.7, 19.86) * mm, "end": v(-49.13, 19.34) * mm});
            skLineSegment(sketch, "E280", {"start": v(-49.13, 19.34) * mm, "end": v(-49.54, 18.8) * mm});
            skLineSegment(sketch, "E281", {"start": v(-49.54, 18.8) * mm, "end": v(-49.94, 18.26) * mm});
            skLineSegment(sketch, "E282", {"start": v(-49.94, 18.26) * mm, "end": v(-50.37, 17.63) * mm});
            skLineSegment(sketch, "E283", {"start": v(-50.37, 17.63) * mm, "end": v(-50.81, 17.03) * mm});
            skLineSegment(sketch, "E284", {"start": v(-50.81, 17.03) * mm, "end": v(-51.26, 16.47) * mm});
            skLineSegment(sketch, "E285", {"start": v(-51.26, 16.47) * mm, "end": v(-51.7, 15.93) * mm});
            skLineSegment(sketch, "E286", {"start": v(-51.7, 15.93) * mm, "end": v(-52.16, 15.43) * mm});
            skLineSegment(sketch, "E287", {"start": v(-52.16, 15.43) * mm, "end": v(-52.62, 14.96) * mm});
            skLineSegment(sketch, "E288", {"start": v(-52.62, 14.96) * mm, "end": v(-53.08, 14.51) * mm});
            skLineSegment(sketch, "E289", {"start": v(-53.08, 14.51) * mm, "end": v(-53.54, 14.1) * mm});
            skLineSegment(sketch, "E290", {"start": v(-53.54, 14.1) * mm, "end": v(-54.01, 13.7) * mm});
            skLineSegment(sketch, "E291", {"start": v(-54.01, 13.7) * mm, "end": v(-54.48, 13.34) * mm});
            skLineSegment(sketch, "E292", {"start": v(-54.48, 13.34) * mm, "end": v(-54.96, 13) * mm});
            skLineSegment(sketch, "E293", {"start": v(-54.96, 13) * mm, "end": v(-55.44, 12.68) * mm});
            skLineSegment(sketch, "E294", {"start": v(-55.44, 12.68) * mm, "end": v(-55.92, 12.39) * mm});
            skLineSegment(sketch, "E295", {"start": v(-55.92, 12.39) * mm, "end": v(-56.4, 12.12) * mm});
            skLineSegment(sketch, "E296", {"start": v(-56.4, 12.12) * mm, "end": v(-56.89, 11.87) * mm});
            skLineSegment(sketch, "E297", {"start": v(-56.89, 11.87) * mm, "end": v(-57.37, 11.64) * mm});
            skLineSegment(sketch, "E298", {"start": v(-57.37, 11.64) * mm, "end": v(-57.87, 11.44) * mm});
            skLineSegment(sketch, "E299", {"start": v(-57.87, 11.44) * mm, "end": v(-58.36, 11.25) * mm});
            skLineSegment(sketch, "E300", {"start": v(-58.36, 11.25) * mm, "end": v(-58.86, 11.08) * mm});
            skLineSegment(sketch, "E301", {"start": v(-58.86, 11.08) * mm, "end": v(-59.36, 10.92) * mm});
            skLineSegment(sketch, "E302", {"start": v(-59.36, 10.92) * mm, "end": v(-59.86, 10.79) * mm});
            skLineSegment(sketch, "E303", {"start": v(-59.86, 10.79) * mm, "end": v(-60.36, 10.67) * mm});
            skLineSegment(sketch, "E304", {"start": v(-60.36, 10.67) * mm, "end": v(-60.87, 10.56) * mm});
            skLineSegment(sketch, "E305", {"start": v(-60.87, 10.56) * mm, "end": v(-61.38, 10.47) * mm});
            skLineSegment(sketch, "E306", {"start": v(-61.38, 10.47) * mm, "end": v(-61.89, 10.4) * mm});
            skLineSegment(sketch, "E307", {"start": v(-61.89, 10.4) * mm, "end": v(-62.4, 10.32) * mm});
            skLineSegment(sketch, "E308", {"start": v(-62.4, 10.32) * mm, "end": v(-62.91, 10.27) * mm});
            skLineSegment(sketch, "E309", {"start": v(-62.91, 10.27) * mm, "end": v(-63.43, 10.23) * mm});
            skLineSegment(sketch, "E310", {"start": v(-63.43, 10.23) * mm, "end": v(-63.94, 10.2) * mm});
            skLineSegment(sketch, "E311", {"start": v(-63.94, 10.2) * mm, "end": v(-64.46, 10.16) * mm});
            skLineSegment(sketch, "E312", {"start": v(-64.46, 10.16) * mm, "end": v(-64.98, 10.15) * mm});
            skLineSegment(sketch, "E313", {"start": v(-64.98, 10.15) * mm, "end": v(-65.5, 10.14) * mm});
            skLineSegment(sketch, "E314", {"start": v(-65.5, 10.14) * mm, "end": v(-65.55, 10.14) * mm});
            skLineSegment(sketch, "E315", {"start": v(-65.55, 10.14) * mm, "end": v(-65.6, 10.13) * mm});
            skLineSegment(sketch, "E316", {"start": v(-65.6, 10.13) * mm, "end": v(-65.64, 10.13) * mm});
            skLineSegment(sketch, "E317", {"start": v(-65.64, 10.13) * mm, "end": v(-65.69, 10.13) * mm});
            skLineSegment(sketch, "E318", {"start": v(-65.69, 10.13) * mm, "end": v(-65.74, 10.13) * mm});
            skLineSegment(sketch, "E319", {"start": v(-65.74, 10.13) * mm, "end": v(-65.78, 10.13) * mm});
            skLineSegment(sketch, "E320", {"start": v(-65.78, 10.13) * mm, "end": v(-65.83, 10.13) * mm});
            skLineSegment(sketch, "E321", {"start": v(-65.83, 10.13) * mm, "end": v(-65.88, 10.13) * mm});
            skLineSegment(sketch, "E322", {"start": v(-65.88, 10.13) * mm, "end": v(-65.93, 10.13) * mm});
            skLineSegment(sketch, "E323", {"start": v(-65.93, 10.13) * mm, "end": v(-65.97, 10.13) * mm});
            skLineSegment(sketch, "E324", {"start": v(-65.97, 10.13) * mm, "end": v(-66.02, 10.13) * mm});
            skLineSegment(sketch, "E325", {"start": v(-66.02, 10.13) * mm, "end": v(-66.07, 10.13) * mm});
            skLineSegment(sketch, "E326", {"start": v(-66.07, 10.13) * mm, "end": v(-66.11, 10.13) * mm});
            skLineSegment(sketch, "E327", {"start": v(-66.11, 10.13) * mm, "end": v(-66.16, 10.13) * mm});
            skLineSegment(sketch, "E328", {"start": v(-66.16, 10.13) * mm, "end": v(-66.2, 10.13) * mm});
            skLineSegment(sketch, "E329", {"start": v(-66.2, 10.13) * mm, "end": v(-66.26, 10.13) * mm});
            skLineSegment(sketch, "E330", {"start": v(-66.26, 10.13) * mm, "end": v(-66.3, 10.13) * mm});
            skLineSegment(sketch, "E331", {"start": v(-66.3, 10.13) * mm, "end": v(-66.35, 10.13) * mm});
            skLineSegment(sketch, "E332", {"start": v(-66.35, 10.13) * mm, "end": v(-66.4, 10.13) * mm});
            skLineSegment(sketch, "E333", {"start": v(-66.4, 10.13) * mm, "end": v(-66.44, 10.13) * mm});
            skLineSegment(sketch, "E334", {"start": v(-66.44, 10.13) * mm, "end": v(-66.5, 10.13) * mm});
            skLineSegment(sketch, "E335", {"start": v(-66.5, 10.13) * mm, "end": v(-66.54, 10.13) * mm});
            skLineSegment(sketch, "E336", {"start": v(-66.54, 10.13) * mm, "end": v(-66.59, 10.13) * mm});
            skLineSegment(sketch, "E337", {"start": v(-66.59, 10.13) * mm, "end": v(-66.63, 10.13) * mm});
            skLineSegment(sketch, "E338", {"start": v(-66.63, 10.13) * mm, "end": v(-66.68, 10.13) * mm});
            skLineSegment(sketch, "E339", {"start": v(-66.68, 10.13) * mm, "end": v(-66.73, 10.13) * mm});
            skLineSegment(sketch, "E340", {"start": v(-66.73, 10.13) * mm, "end": v(-66.78, 10.13) * mm});
            skLineSegment(sketch, "E341", {"start": v(-66.78, 10.13) * mm, "end": v(-66.82, 10.13) * mm});
            skLineSegment(sketch, "E342", {"start": v(-66.82, 10.13) * mm, "end": v(-66.87, 10.13) * mm});
            skLineSegment(sketch, "E343", {"start": v(-66.87, 10.13) * mm, "end": v(-66.92, 10.13) * mm});
            skLineSegment(sketch, "E344", {"start": v(-66.92, 10.13) * mm, "end": v(-66.96, 10.13) * mm});
            skLineSegment(sketch, "E345", {"start": v(-66.96, 10.13) * mm, "end": v(-67.01, 10.13) * mm});
            skLineSegment(sketch, "E346", {"start": v(-67.01, 10.13) * mm, "end": v(-67.01, 10.13) * mm});
            skLineSegment(sketch, "E347", {"start": v(-67.01, 10.13) * mm, "end": v(-67.1, 10.12) * mm});
            skLineSegment(sketch, "E348", {"start": v(-67.1, 10.12) * mm, "end": v(-67.2, 10.12) * mm});
            skLineSegment(sketch, "E349", {"start": v(-67.2, 10.12) * mm, "end": v(-67.29, 10.1) * mm});
            skLineSegment(sketch, "E350", {"start": v(-67.29, 10.1) * mm, "end": v(-67.38, 10.09) * mm});
            skLineSegment(sketch, "E351", {"start": v(-67.38, 10.09) * mm, "end": v(-67.46, 10.07) * mm});
            skLineSegment(sketch, "E352", {"start": v(-67.46, 10.07) * mm, "end": v(-67.55, 10.04) * mm});
            skLineSegment(sketch, "E353", {"start": v(-67.55, 10.04) * mm, "end": v(-67.63, 10.02) * mm});
            skLineSegment(sketch, "E354", {"start": v(-67.63, 10.02) * mm, "end": v(-67.72, 9.98) * mm});
            skLineSegment(sketch, "E355", {"start": v(-67.72, 9.98) * mm, "end": v(-67.8, 9.95) * mm});
            skLineSegment(sketch, "E356", {"start": v(-67.8, 9.95) * mm, "end": v(-67.87, 9.9) * mm});
            skLineSegment(sketch, "E357", {"start": v(-67.87, 9.9) * mm, "end": v(-67.95, 9.86) * mm});
            skLineSegment(sketch, "E358", {"start": v(-67.95, 9.86) * mm, "end": v(-68.02, 9.82) * mm});
            skLineSegment(sketch, "E359", {"start": v(-68.02, 9.82) * mm, "end": v(-68.1, 9.77) * mm});
            skLineSegment(sketch, "E360", {"start": v(-68.1, 9.77) * mm, "end": v(-68.16, 9.71) * mm});
            skLineSegment(sketch, "E361", {"start": v(-68.16, 9.71) * mm, "end": v(-68.23, 9.65) * mm});
            skLineSegment(sketch, "E362", {"start": v(-68.23, 9.65) * mm, "end": v(-68.3, 9.6) * mm});
            skLineSegment(sketch, "E363", {"start": v(-68.3, 9.6) * mm, "end": v(-68.35, 9.53) * mm});
            skLineSegment(sketch, "E364", {"start": v(-68.35, 9.53) * mm, "end": v(-68.4, 9.47) * mm});
            skLineSegment(sketch, "E365", {"start": v(-68.4, 9.47) * mm, "end": v(-68.46, 9.4) * mm});
            skLineSegment(sketch, "E366", {"start": v(-68.46, 9.4) * mm, "end": v(-68.51, 9.33) * mm});
            skLineSegment(sketch, "E367", {"start": v(-68.51, 9.33) * mm, "end": v(-68.56, 9.25) * mm});
            skLineSegment(sketch, "E368", {"start": v(-68.56, 9.25) * mm, "end": v(-68.6, 9.18) * mm});
            skLineSegment(sketch, "E369", {"start": v(-68.6, 9.18) * mm, "end": v(-68.64, 9.1) * mm});
            skLineSegment(sketch, "E370", {"start": v(-68.64, 9.1) * mm, "end": v(-68.68, 9.02) * mm});
            skLineSegment(sketch, "E371", {"start": v(-68.68, 9.02) * mm, "end": v(-68.71, 8.94) * mm});
            skLineSegment(sketch, "E372", {"start": v(-68.71, 8.94) * mm, "end": v(-68.74, 8.85) * mm});
            skLineSegment(sketch, "E373", {"start": v(-68.74, 8.85) * mm, "end": v(-68.77, 8.77) * mm});
            skLineSegment(sketch, "E374", {"start": v(-68.77, 8.77) * mm, "end": v(-68.79, 8.68) * mm});
            skLineSegment(sketch, "E375", {"start": v(-68.79, 8.68) * mm, "end": v(-68.8, 8.59) * mm});
            skLineSegment(sketch, "E376", {"start": v(-68.8, 8.59) * mm, "end": v(-68.81, 8.5) * mm});
            skLineSegment(sketch, "E377", {"start": v(-68.81, 8.5) * mm, "end": v(-68.82, 8.4) * mm});
            skLineSegment(sketch, "E378", {"start": v(-68.82, 8.4) * mm, "end": v(-68.82, 8.31) * mm});
            skLineSegment(sketch, "E379", {"start": v(-68.82, 8.31) * mm, "end": v(-68.82, 8.22) * mm});
            skLineSegment(sketch, "E380", {"start": v(-68.82, 8.22) * mm, "end": v(-68.81, 8.13) * mm});
            skLineSegment(sketch, "E381", {"start": v(-68.81, 8.13) * mm, "end": v(-68.8, 8.04) * mm});
            skLineSegment(sketch, "E382", {"start": v(-68.8, 8.04) * mm, "end": v(-68.79, 7.95) * mm});
            skLineSegment(sketch, "E383", {"start": v(-68.79, 7.95) * mm, "end": v(-68.77, 7.86) * mm});
            skLineSegment(sketch, "E384", {"start": v(-68.77, 7.86) * mm, "end": v(-68.74, 7.77) * mm});
            skLineSegment(sketch, "E385", {"start": v(-68.74, 7.77) * mm, "end": v(-68.71, 7.7) * mm});
            skLineSegment(sketch, "E386", {"start": v(-68.71, 7.7) * mm, "end": v(-68.68, 7.6) * mm});
            skLineSegment(sketch, "E387", {"start": v(-68.68, 7.6) * mm, "end": v(-68.64, 7.53) * mm});
            skLineSegment(sketch, "E388", {"start": v(-68.64, 7.53) * mm, "end": v(-68.6, 7.45) * mm});
            skLineSegment(sketch, "E389", {"start": v(-68.6, 7.45) * mm, "end": v(-68.56, 7.37) * mm});
            skLineSegment(sketch, "E390", {"start": v(-68.56, 7.37) * mm, "end": v(-68.51, 7.3) * mm});
            skLineSegment(sketch, "E391", {"start": v(-68.51, 7.3) * mm, "end": v(-68.46, 7.23) * mm});
            skLineSegment(sketch, "E392", {"start": v(-68.46, 7.23) * mm, "end": v(-68.4, 7.16) * mm});
            skLineSegment(sketch, "E393", {"start": v(-68.4, 7.16) * mm, "end": v(-68.35, 7.1) * mm});
            skLineSegment(sketch, "E394", {"start": v(-68.35, 7.1) * mm, "end": v(-68.3, 7.03) * mm});
            skLineSegment(sketch, "E395", {"start": v(-68.3, 7.03) * mm, "end": v(-68.23, 6.97) * mm});
            skLineSegment(sketch, "E396", {"start": v(-68.23, 6.97) * mm, "end": v(-68.16, 6.91) * mm});
            skLineSegment(sketch, "E397", {"start": v(-68.16, 6.91) * mm, "end": v(-68.1, 6.86) * mm});
            skLineSegment(sketch, "E398", {"start": v(-68.1, 6.86) * mm, "end": v(-68.02, 6.81) * mm});
            skLineSegment(sketch, "E399", {"start": v(-68.02, 6.81) * mm, "end": v(-67.95, 6.76) * mm});
            skLineSegment(sketch, "E400", {"start": v(-67.95, 6.76) * mm, "end": v(-67.87, 6.72) * mm});
            skLineSegment(sketch, "E401", {"start": v(-67.87, 6.72) * mm, "end": v(-67.8, 6.68) * mm});
            skLineSegment(sketch, "E402", {"start": v(-67.8, 6.68) * mm, "end": v(-67.72, 6.64) * mm});
            skLineSegment(sketch, "E403", {"start": v(-67.72, 6.64) * mm, "end": v(-67.63, 6.61) * mm});
            skLineSegment(sketch, "E404", {"start": v(-67.63, 6.61) * mm, "end": v(-67.55, 6.58) * mm});
            skLineSegment(sketch, "E405", {"start": v(-67.55, 6.58) * mm, "end": v(-67.46, 6.56) * mm});
            skLineSegment(sketch, "E406", {"start": v(-67.46, 6.56) * mm, "end": v(-67.38, 6.54) * mm});
            skLineSegment(sketch, "E407", {"start": v(-67.38, 6.54) * mm, "end": v(-67.29, 6.52) * mm});
            skLineSegment(sketch, "E408", {"start": v(-67.29, 6.52) * mm, "end": v(-67.2, 6.51) * mm});
            skLineSegment(sketch, "E409", {"start": v(-67.2, 6.51) * mm, "end": v(-67.1, 6.5) * mm});
            skLineSegment(sketch, "E410", {"start": v(-67.1, 6.5) * mm, "end": v(-67.01, 6.5) * mm});
            skLineSegment(sketch, "E411", {"start": v(-67.01, 6.5) * mm, "end": v(-67.01, 6.5) * mm});
            skLineSegment(sketch, "E412", {"start": v(-67.01, 6.5) * mm, "end": v(-65.79, 6.49) * mm});
            skLineSegment(sketch, "E413", {"start": v(-65.79, 6.49) * mm, "end": v(-64.65, 6.44) * mm});
            skLineSegment(sketch, "E414", {"start": v(-64.65, 6.44) * mm, "end": v(-63.6, 6.37) * mm});
            skLineSegment(sketch, "E415", {"start": v(-63.6, 6.37) * mm, "end": v(-62.62, 6.27) * mm});
            skLineSegment(sketch, "E416", {"start": v(-62.62, 6.27) * mm, "end": v(-61.71, 6.14) * mm});
            skLineSegment(sketch, "E417", {"start": v(-61.71, 6.14) * mm, "end": v(-60.88, 5.99) * mm});
            skLineSegment(sketch, "E418", {"start": v(-60.88, 5.99) * mm, "end": v(-60.12, 5.8) * mm});
            skLineSegment(sketch, "E419", {"start": v(-60.12, 5.8) * mm, "end": v(-59.41, 5.6) * mm});
            skLineSegment(sketch, "E420", {"start": v(-59.41, 5.6) * mm, "end": v(-58.77, 5.37) * mm});
            skLineSegment(sketch, "E421", {"start": v(-58.77, 5.37) * mm, "end": v(-58.18, 5.11) * mm});
            skLineSegment(sketch, "E422", {"start": v(-58.18, 5.11) * mm, "end": v(-57.64, 4.83) * mm});
            skLineSegment(sketch, "E423", {"start": v(-57.64, 4.83) * mm, "end": v(-57.15, 4.53) * mm});
            skLineSegment(sketch, "E424", {"start": v(-57.15, 4.53) * mm, "end": v(-56.7, 4.2) * mm});
            skLineSegment(sketch, "E425", {"start": v(-56.7, 4.2) * mm, "end": v(-56.3, 3.85) * mm});
            skLineSegment(sketch, "E426", {"start": v(-56.3, 3.85) * mm, "end": v(-55.92, 3.48) * mm});
            skLineSegment(sketch, "E427", {"start": v(-55.92, 3.48) * mm, "end": v(-55.57, 3.09) * mm});
            skLineSegment(sketch, "E428", {"start": v(-55.57, 3.09) * mm, "end": v(-55.26, 2.67) * mm});
            skLineSegment(sketch, "E429", {"start": v(-55.26, 2.67) * mm, "end": v(-54.97, 2.24) * mm});
            skLineSegment(sketch, "E430", {"start": v(-54.97, 2.24) * mm, "end": v(-54.7, 1.78) * mm});
            skLineSegment(sketch, "E431", {"start": v(-54.7, 1.78) * mm, "end": v(-54.44, 1.31) * mm});
            skLineSegment(sketch, "E432", {"start": v(-54.44, 1.31) * mm, "end": v(-54.2, 0.82) * mm});
            skLineSegment(sketch, "E433", {"start": v(-54.2, 0.82) * mm, "end": v(-53.96, 0.3) * mm});
            skLineSegment(sketch, "E434", {"start": v(-53.96, 0.3) * mm, "end": v(-53.73, -0.22) * mm});
            skLineSegment(sketch, "E435", {"start": v(-53.73, -0.22) * mm, "end": v(-53.5, -0.77) * mm});
            skLineSegment(sketch, "E436", {"start": v(-53.5, -0.77) * mm, "end": v(-53.26, -1.33) * mm});
            skLineSegment(sketch, "E437", {"start": v(-53.26, -1.33) * mm, "end": v(-53.01, -1.91) * mm});
            skLineSegment(sketch, "E438", {"start": v(-53.01, -1.91) * mm, "end": v(-52.76, -2.5) * mm});
            skLineSegment(sketch, "E439", {"start": v(-52.76, -2.5) * mm, "end": v(-52.49, -3.11) * mm});
            skLineSegment(sketch, "E440", {"start": v(-52.49, -3.11) * mm, "end": v(-52.2, -3.74) * mm});
            skLineSegment(sketch, "E441", {"start": v(-52.2, -3.74) * mm, "end": v(-51.89, -4.38) * mm});
            skLineSegment(sketch, "E442", {"start": v(-51.89, -4.38) * mm, "end": v(-51.55, -5.03) * mm});
            skLineSegment(sketch, "E443", {"start": v(-51.55, -5.03) * mm, "end": v(-51.17, -5.7) * mm});
            skLineSegment(sketch, "E444", {"start": v(-51.17, -5.7) * mm, "end": v(-51.15, -5.73) * mm});
            skLineSegment(sketch, "E445", {"start": v(-51.15, -5.73) * mm, "end": v(-51.14, -5.77) * mm});
            skLineSegment(sketch, "E446", {"start": v(-51.14, -5.77) * mm, "end": v(-51.12, -5.8) * mm});
            skLineSegment(sketch, "E447", {"start": v(-51.12, -5.8) * mm, "end": v(-51.1, -5.84) * mm});
            skLineSegment(sketch, "E448", {"start": v(-51.1, -5.84) * mm, "end": v(-51.08, -5.87) * mm});
            skLineSegment(sketch, "E449", {"start": v(-51.08, -5.87) * mm, "end": v(-51.06, -5.9) * mm});
            skLineSegment(sketch, "E450", {"start": v(-51.06, -5.9) * mm, "end": v(-51.04, -5.94) * mm});
            skLineSegment(sketch, "E451", {"start": v(-51.04, -5.94) * mm, "end": v(-51.02, -5.98) * mm});
            skLineSegment(sketch, "E452", {"start": v(-51.02, -5.98) * mm, "end": v(-51, -6.01) * mm});
            skLineSegment(sketch, "E453", {"start": v(-51, -6.01) * mm, "end": v(-50.98, -6.04) * mm});
            skLineSegment(sketch, "E454", {"start": v(-50.98, -6.04) * mm, "end": v(-50.96, -6.08) * mm});
            skLineSegment(sketch, "E455", {"start": v(-50.96, -6.08) * mm, "end": v(-50.94, -6.11) * mm});
            skLineSegment(sketch, "E456", {"start": v(-50.94, -6.11) * mm, "end": v(-50.91, -6.15) * mm});
            skLineSegment(sketch, "E457", {"start": v(-50.91, -6.15) * mm, "end": v(-50.9, -6.18) * mm});
            skLineSegment(sketch, "E458", {"start": v(-50.9, -6.18) * mm, "end": v(-50.87, -6.22) * mm});
            skLineSegment(sketch, "E459", {"start": v(-50.87, -6.22) * mm, "end": v(-50.85, -6.25) * mm});
            skLineSegment(sketch, "E460", {"start": v(-50.85, -6.25) * mm, "end": v(-50.83, -6.29) * mm});
            skLineSegment(sketch, "E461", {"start": v(-50.83, -6.29) * mm, "end": v(-50.81, -6.32) * mm});
            skLineSegment(sketch, "E462", {"start": v(-50.81, -6.32) * mm, "end": v(-50.8, -6.36) * mm});
            skLineSegment(sketch, "E463", {"start": v(-50.8, -6.36) * mm, "end": v(-50.77, -6.4) * mm});
            skLineSegment(sketch, "E464", {"start": v(-50.77, -6.4) * mm, "end": v(-50.75, -6.42) * mm});
            skLineSegment(sketch, "E465", {"start": v(-50.75, -6.42) * mm, "end": v(-50.73, -6.46) * mm});
            skLineSegment(sketch, "E466", {"start": v(-50.73, -6.46) * mm, "end": v(-50.7, -6.5) * mm});
            skLineSegment(sketch, "E467", {"start": v(-50.7, -6.5) * mm, "end": v(-50.69, -6.53) * mm});
            skLineSegment(sketch, "E468", {"start": v(-50.69, -6.53) * mm, "end": v(-50.67, -6.56) * mm});
            skLineSegment(sketch, "E469", {"start": v(-50.67, -6.56) * mm, "end": v(-50.65, -6.6) * mm});
            skLineSegment(sketch, "E470", {"start": v(-50.65, -6.6) * mm, "end": v(-50.62, -6.63) * mm});
            skLineSegment(sketch, "E471", {"start": v(-50.62, -6.63) * mm, "end": v(-50.6, -6.66) * mm});
            skLineSegment(sketch, "E472", {"start": v(-50.6, -6.66) * mm, "end": v(-50.58, -6.7) * mm});
            skLineSegment(sketch, "E473", {"start": v(-50.58, -6.7) * mm, "end": v(-50.56, -6.73) * mm});
            skLineSegment(sketch, "E474", {"start": v(-50.56, -6.73) * mm, "end": v(-50.54, -6.77) * mm});
            skLineSegment(sketch, "E475", {"start": v(-50.54, -6.77) * mm, "end": v(-50.52, -6.8) * mm});
            skLineSegment(sketch, "E476", {"start": v(-50.52, -6.8) * mm, "end": v(-50.13, -7.44) * mm});
            skLineSegment(sketch, "E477", {"start": v(-50.13, -7.44) * mm, "end": v(-49.78, -8.08) * mm});
            skLineSegment(sketch, "E478", {"start": v(-49.78, -8.08) * mm, "end": v(-49.45, -8.7) * mm});
            skLineSegment(sketch, "E479", {"start": v(-49.45, -8.7) * mm, "end": v(-49.16, -9.32) * mm});
            skLineSegment(sketch, "E480", {"start": v(-49.16, -9.32) * mm, "end": v(-48.89, -9.93) * mm});
            skLineSegment(sketch, "E481", {"start": v(-48.89, -9.93) * mm, "end": v(-48.65, -10.53) * mm});
            skLineSegment(sketch, "E482", {"start": v(-48.65, -10.53) * mm, "end": v(-48.44, -11.12) * mm});
            skLineSegment(sketch, "E483", {"start": v(-48.44, -11.12) * mm, "end": v(-48.25, -11.7) * mm});
            skLineSegment(sketch, "E484", {"start": v(-48.25, -11.7) * mm, "end": v(-48.09, -12.28) * mm});
            skLineSegment(sketch, "E485", {"start": v(-48.09, -12.28) * mm, "end": v(-47.95, -12.85) * mm});
            skLineSegment(sketch, "E486", {"start": v(-47.95, -12.85) * mm, "end": v(-47.83, -13.42) * mm});
            skLineSegment(sketch, "E487", {"start": v(-47.83, -13.42) * mm, "end": v(-47.74, -13.97) * mm});
            skLineSegment(sketch, "E488", {"start": v(-47.74, -13.97) * mm, "end": v(-47.67, -14.52) * mm});
            skLineSegment(sketch, "E489", {"start": v(-47.67, -14.52) * mm, "end": v(-47.62, -15.07) * mm});
            skLineSegment(sketch, "E490", {"start": v(-47.62, -15.07) * mm, "end": v(-47.6, -15.6) * mm});
            skLineSegment(sketch, "E491", {"start": v(-47.6, -15.6) * mm, "end": v(-47.59, -16.14) * mm});
            skLineSegment(sketch, "E492", {"start": v(-47.59, -16.14) * mm, "end": v(-47.6, -16.67) * mm});
            skLineSegment(sketch, "E493", {"start": v(-47.6, -16.67) * mm, "end": v(-47.63, -17.19) * mm});
            skLineSegment(sketch, "E494", {"start": v(-47.63, -17.19) * mm, "end": v(-47.67, -17.7) * mm});
            skLineSegment(sketch, "E495", {"start": v(-47.67, -17.7) * mm, "end": v(-47.74, -18.22) * mm});
            skLineSegment(sketch, "E496", {"start": v(-47.74, -18.22) * mm, "end": v(-47.81, -18.73) * mm});
            skLineSegment(sketch, "E497", {"start": v(-47.81, -18.73) * mm, "end": v(-47.9, -19.23) * mm});
            skLineSegment(sketch, "E498", {"start": v(-47.9, -19.23) * mm, "end": v(-48.01, -19.73) * mm});
            skLineSegment(sketch, "E499", {"start": v(-48.01, -19.73) * mm, "end": v(-48.13, -20.23) * mm});
            skLineSegment(sketch, "E500", {"start": v(-48.13, -20.23) * mm, "end": v(-48.27, -20.72) * mm});
            skLineSegment(sketch, "E501", {"start": v(-48.27, -20.72) * mm, "end": v(-48.4, -21.21) * mm});
            skLineSegment(sketch, "E502", {"start": v(-48.4, -21.21) * mm, "end": v(-48.56, -21.7) * mm});
            skLineSegment(sketch, "E503", {"start": v(-48.56, -21.7) * mm, "end": v(-48.73, -22.18) * mm});
            skLineSegment(sketch, "E504", {"start": v(-48.73, -22.18) * mm, "end": v(-48.9, -22.66) * mm});
            skLineSegment(sketch, "E505", {"start": v(-48.9, -22.66) * mm, "end": v(-49.09, -23.14) * mm});
            skLineSegment(sketch, "E506", {"start": v(-49.09, -23.14) * mm, "end": v(-49.28, -23.62) * mm});
            skLineSegment(sketch, "E507", {"start": v(-49.28, -23.62) * mm, "end": v(-49.47, -24.1) * mm});
            skLineSegment(sketch, "E508", {"start": v(-49.47, -24.1) * mm, "end": v(-49.5, -24.14) * mm});
            skLineSegment(sketch, "E509", {"start": v(-49.5, -24.14) * mm, "end": v(-49.51, -24.18) * mm});
            skLineSegment(sketch, "E510", {"start": v(-49.51, -24.18) * mm, "end": v(-49.53, -24.23) * mm});
            skLineSegment(sketch, "E511", {"start": v(-49.53, -24.23) * mm, "end": v(-49.55, -24.27) * mm});
            skLineSegment(sketch, "E512", {"start": v(-49.55, -24.27) * mm, "end": v(-49.57, -24.31) * mm});
            skLineSegment(sketch, "E513", {"start": v(-49.57, -24.31) * mm, "end": v(-49.59, -24.36) * mm});
            skLineSegment(sketch, "E514", {"start": v(-49.59, -24.36) * mm, "end": v(-49.6, -24.4) * mm});
            skLineSegment(sketch, "E515", {"start": v(-49.6, -24.4) * mm, "end": v(-49.62, -24.44) * mm});
            skLineSegment(sketch, "E516", {"start": v(-49.62, -24.44) * mm, "end": v(-49.64, -24.49) * mm});
            skLineSegment(sketch, "E517", {"start": v(-49.64, -24.49) * mm, "end": v(-49.66, -24.53) * mm});
            skLineSegment(sketch, "E518", {"start": v(-49.66, -24.53) * mm, "end": v(-49.68, -24.57) * mm});
            skLineSegment(sketch, "E519", {"start": v(-49.68, -24.57) * mm, "end": v(-49.7, -24.62) * mm});
            skLineSegment(sketch, "E520", {"start": v(-49.7, -24.62) * mm, "end": v(-49.72, -24.66) * mm});
            skLineSegment(sketch, "E521", {"start": v(-49.72, -24.66) * mm, "end": v(-49.74, -24.7) * mm});
            skLineSegment(sketch, "E522", {"start": v(-49.74, -24.7) * mm, "end": v(-49.75, -24.75) * mm});
            skLineSegment(sketch, "E523", {"start": v(-49.75, -24.75) * mm, "end": v(-49.77, -24.79) * mm});
            skLineSegment(sketch, "E524", {"start": v(-49.77, -24.79) * mm, "end": v(-49.8, -24.83) * mm});
            skLineSegment(sketch, "E525", {"start": v(-49.8, -24.83) * mm, "end": v(-49.81, -24.88) * mm});
            skLineSegment(sketch, "E526", {"start": v(-49.81, -24.88) * mm, "end": v(-49.83, -24.92) * mm});
            skLineSegment(sketch, "E527", {"start": v(-49.83, -24.92) * mm, "end": v(-49.85, -24.96) * mm});
            skLineSegment(sketch, "E528", {"start": v(-49.85, -24.96) * mm, "end": v(-49.87, -25) * mm});
            skLineSegment(sketch, "E529", {"start": v(-49.87, -25) * mm, "end": v(-49.89, -25.05) * mm});
            skLineSegment(sketch, "E530", {"start": v(-49.89, -25.05) * mm, "end": v(-49.9, -25.1) * mm});
            skLineSegment(sketch, "E531", {"start": v(-49.9, -25.1) * mm, "end": v(-49.92, -25.14) * mm});
            skLineSegment(sketch, "E532", {"start": v(-49.92, -25.14) * mm, "end": v(-49.94, -25.18) * mm});
            skLineSegment(sketch, "E533", {"start": v(-49.94, -25.18) * mm, "end": v(-49.96, -25.22) * mm});
            skLineSegment(sketch, "E534", {"start": v(-49.96, -25.22) * mm, "end": v(-49.98, -25.27) * mm});
            skLineSegment(sketch, "E535", {"start": v(-49.98, -25.27) * mm, "end": v(-50, -25.3) * mm});
            skLineSegment(sketch, "E536", {"start": v(-50, -25.3) * mm, "end": v(-50.02, -25.35) * mm});
            skLineSegment(sketch, "E537", {"start": v(-50.02, -25.35) * mm, "end": v(-50.04, -25.4) * mm});
            skLineSegment(sketch, "E538", {"start": v(-50.04, -25.4) * mm, "end": v(-50.05, -25.44) * mm});
            skLineSegment(sketch, "E539", {"start": v(-50.05, -25.44) * mm, "end": v(-50.07, -25.48) * mm});
            skLineSegment(sketch, "E540", {"start": v(-50.07, -25.48) * mm, "end": v(-50.07, -25.48) * mm});
            skLineSegment(sketch, "E541", {"start": v(-50.07, -25.48) * mm, "end": v(-50.1, -25.57) * mm});
            skLineSegment(sketch, "E542", {"start": v(-50.1, -25.57) * mm, "end": v(-50.14, -25.66) * mm});
            skLineSegment(sketch, "E543", {"start": v(-50.14, -25.66) * mm, "end": v(-50.16, -25.74) * mm});
            skLineSegment(sketch, "E544", {"start": v(-50.16, -25.74) * mm, "end": v(-50.18, -25.83) * mm});
            skLineSegment(sketch, "E545", {"start": v(-50.18, -25.83) * mm, "end": v(-50.2, -25.92) * mm});
            skLineSegment(sketch, "E546", {"start": v(-50.2, -25.92) * mm, "end": v(-50.21, -26) * mm});
            skLineSegment(sketch, "E547", {"start": v(-50.21, -26) * mm, "end": v(-50.22, -26.1) * mm});
            skLineSegment(sketch, "E548", {"start": v(-50.22, -26.1) * mm, "end": v(-50.22, -26.19) * mm});
            skLineSegment(sketch, "E549", {"start": v(-50.22, -26.19) * mm, "end": v(-50.22, -26.27) * mm});
            skLineSegment(sketch, "E550", {"start": v(-50.22, -26.27) * mm, "end": v(-50.22, -26.36) * mm});
            skLineSegment(sketch, "E551", {"start": v(-50.22, -26.36) * mm, "end": v(-50.2, -26.45) * mm});
            skLineSegment(sketch, "E552", {"start": v(-50.2, -26.45) * mm, "end": v(-50.2, -26.53) * mm});
            skLineSegment(sketch, "E553", {"start": v(-50.2, -26.53) * mm, "end": v(-50.18, -26.62) * mm});
            skLineSegment(sketch, "E554", {"start": v(-50.18, -26.62) * mm, "end": v(-50.16, -26.7) * mm});
            skLineSegment(sketch, "E555", {"start": v(-50.16, -26.7) * mm, "end": v(-50.13, -26.79) * mm});
            skLineSegment(sketch, "E556", {"start": v(-50.13, -26.79) * mm, "end": v(-50.1, -26.87) * mm});
            skLineSegment(sketch, "E557", {"start": v(-50.1, -26.87) * mm, "end": v(-50.07, -26.95) * mm});
            skLineSegment(sketch, "E558", {"start": v(-50.07, -26.95) * mm, "end": v(-50.03, -27.03) * mm});
            skLineSegment(sketch, "E559", {"start": v(-50.03, -27.03) * mm, "end": v(-49.99, -27.1) * mm});
            skLineSegment(sketch, "E560", {"start": v(-49.99, -27.1) * mm, "end": v(-49.94, -27.18) * mm});
            skLineSegment(sketch, "E561", {"start": v(-49.94, -27.18) * mm, "end": v(-49.9, -27.25) * mm});
            skLineSegment(sketch, "E562", {"start": v(-49.9, -27.25) * mm, "end": v(-49.84, -27.32) * mm});
            skLineSegment(sketch, "E563", {"start": v(-49.84, -27.32) * mm, "end": v(-49.79, -27.4) * mm});
            skLineSegment(sketch, "E564", {"start": v(-49.79, -27.4) * mm, "end": v(-49.73, -27.46) * mm});
            skLineSegment(sketch, "E565", {"start": v(-49.73, -27.46) * mm, "end": v(-49.67, -27.52) * mm});
            skLineSegment(sketch, "E566", {"start": v(-49.67, -27.52) * mm, "end": v(-49.6, -27.58) * mm});
            skLineSegment(sketch, "E567", {"start": v(-49.6, -27.58) * mm, "end": v(-49.53, -27.64) * mm});
            skLineSegment(sketch, "E568", {"start": v(-49.53, -27.64) * mm, "end": v(-49.46, -27.7) * mm});
            skLineSegment(sketch, "E569", {"start": v(-49.46, -27.7) * mm, "end": v(-49.38, -27.74) * mm});
            skLineSegment(sketch, "E570", {"start": v(-49.38, -27.74) * mm, "end": v(-49.3, -27.79) * mm});
            skLineSegment(sketch, "E571", {"start": v(-49.3, -27.79) * mm, "end": v(-49.23, -27.83) * mm});
            skLineSegment(sketch, "E572", {"start": v(-49.23, -27.83) * mm, "end": v(-49.14, -27.87) * mm});
            skLineSegment(sketch, "E573", {"start": v(-49.14, -27.87) * mm, "end": v(-49.05, -27.9) * mm});
            skLineSegment(sketch, "E574", {"start": v(-49.05, -27.9) * mm, "end": v(-48.97, -27.94) * mm});
            skLineSegment(sketch, "E575", {"start": v(-48.97, -27.94) * mm, "end": v(-48.88, -27.96) * mm});
            skLineSegment(sketch, "E576", {"start": v(-48.88, -27.96) * mm, "end": v(-48.8, -27.98) * mm});
            skLineSegment(sketch, "E577", {"start": v(-48.8, -27.98) * mm, "end": v(-48.7, -28) * mm});
            skLineSegment(sketch, "E578", {"start": v(-48.7, -28) * mm, "end": v(-48.61, -28.01) * mm});
            skLineSegment(sketch, "E579", {"start": v(-48.61, -28.01) * mm, "end": v(-48.53, -28.02) * mm});
            skLineSegment(sketch, "E580", {"start": v(-48.53, -28.02) * mm, "end": v(-48.44, -28.02) * mm});
            skLineSegment(sketch, "E581", {"start": v(-48.44, -28.02) * mm, "end": v(-48.35, -28.02) * mm});
            skLineSegment(sketch, "E582", {"start": v(-48.35, -28.02) * mm, "end": v(-48.26, -28.02) * mm});
            skLineSegment(sketch, "E583", {"start": v(-48.26, -28.02) * mm, "end": v(-48.18, -28) * mm});
            skLineSegment(sketch, "E584", {"start": v(-48.18, -28) * mm, "end": v(-48.09, -28) * mm});
            skLineSegment(sketch, "E585", {"start": v(-48.09, -28) * mm, "end": v(-48, -27.98) * mm});
            skLineSegment(sketch, "E586", {"start": v(-48, -27.98) * mm, "end": v(-47.92, -27.96) * mm});
            skLineSegment(sketch, "E587", {"start": v(-47.92, -27.96) * mm, "end": v(-47.84, -27.93) * mm});
            skLineSegment(sketch, "E588", {"start": v(-47.84, -27.93) * mm, "end": v(-47.75, -27.9) * mm});
            skLineSegment(sketch, "E589", {"start": v(-47.75, -27.9) * mm, "end": v(-47.67, -27.87) * mm});
            skLineSegment(sketch, "E590", {"start": v(-47.67, -27.87) * mm, "end": v(-47.6, -27.83) * mm});
            skLineSegment(sketch, "E591", {"start": v(-47.6, -27.83) * mm, "end": v(-47.52, -27.79) * mm});
            skLineSegment(sketch, "E592", {"start": v(-47.52, -27.79) * mm, "end": v(-47.44, -27.74) * mm});
            skLineSegment(sketch, "E593", {"start": v(-47.44, -27.74) * mm, "end": v(-47.37, -27.7) * mm});
            skLineSegment(sketch, "E594", {"start": v(-47.37, -27.7) * mm, "end": v(-47.3, -27.64) * mm});
            skLineSegment(sketch, "E595", {"start": v(-47.3, -27.64) * mm, "end": v(-47.23, -27.59) * mm});
            skLineSegment(sketch, "E596", {"start": v(-47.23, -27.59) * mm, "end": v(-47.17, -27.53) * mm});
            skLineSegment(sketch, "E597", {"start": v(-47.17, -27.53) * mm, "end": v(-47.1, -27.47) * mm});
            skLineSegment(sketch, "E598", {"start": v(-47.1, -27.47) * mm, "end": v(-47.04, -27.4) * mm});
            skLineSegment(sketch, "E599", {"start": v(-47.04, -27.4) * mm, "end": v(-46.99, -27.33) * mm});
            skLineSegment(sketch, "E600", {"start": v(-46.99, -27.33) * mm, "end": v(-46.93, -27.26) * mm});
            skLineSegment(sketch, "E601", {"start": v(-46.93, -27.26) * mm, "end": v(-46.88, -27.18) * mm});
            skLineSegment(sketch, "E602", {"start": v(-46.88, -27.18) * mm, "end": v(-46.84, -27.1) * mm});
            skLineSegment(sketch, "E603", {"start": v(-46.84, -27.1) * mm, "end": v(-46.8, -27.02) * mm});
            skLineSegment(sketch, "E604", {"start": v(-46.8, -27.02) * mm, "end": v(-46.75, -26.94) * mm});
            skLineSegment(sketch, "E605", {"start": v(-46.75, -26.94) * mm, "end": v(-46.75, -26.94) * mm});
            skLineSegment(sketch, "E606", {"start": v(-46.75, -26.94) * mm, "end": v(-46.25, -25.84) * mm});
            skLineSegment(sketch, "E607", {"start": v(-46.25, -25.84) * mm, "end": v(-45.76, -24.83) * mm});
            skLineSegment(sketch, "E608", {"start": v(-45.76, -24.83) * mm, "end": v(-45.28, -23.9) * mm});
            skLineSegment(sketch, "E609", {"start": v(-45.28, -23.9) * mm, "end": v(-44.8, -23.06) * mm});
            skLineSegment(sketch, "E610", {"start": v(-44.8, -23.06) * mm, "end": v(-44.33, -22.3) * mm});
            skLineSegment(sketch, "E611", {"start": v(-44.33, -22.3) * mm, "end": v(-43.86, -21.6) * mm});
            skLineSegment(sketch, "E612", {"start": v(-43.86, -21.6) * mm, "end": v(-43.4, -20.97) * mm});
            skLineSegment(sketch, "E613", {"start": v(-43.4, -20.97) * mm, "end": v(-42.93, -20.4) * mm});
            skLineSegment(sketch, "E614", {"start": v(-42.93, -20.4) * mm, "end": v(-42.47, -19.91) * mm});
            skLineSegment(sketch, "E615", {"start": v(-42.47, -19.91) * mm, "end": v(-42, -19.47) * mm});
            skLineSegment(sketch, "E616", {"start": v(-42, -19.47) * mm, "end": v(-41.54, -19.1) * mm});
            skLineSegment(sketch, "E617", {"start": v(-41.54, -19.1) * mm, "end": v(-41.07, -18.76) * mm});
            skLineSegment(sketch, "E618", {"start": v(-41.07, -18.76) * mm, "end": v(-40.6, -18.47) * mm});
            skLineSegment(sketch, "E619", {"start": v(-40.6, -18.47) * mm, "end": v(-40.12, -18.24) * mm});
            skLineSegment(sketch, "E620", {"start": v(-40.12, -18.24) * mm, "end": v(-39.64, -18.04) * mm});
            skLineSegment(sketch, "E621", {"start": v(-39.64, -18.04) * mm, "end": v(-39.15, -17.87) * mm});
            skLineSegment(sketch, "E622", {"start": v(-39.15, -17.87) * mm, "end": v(-38.66, -17.75) * mm});
            skLineSegment(sketch, "E623", {"start": v(-38.66, -17.75) * mm, "end": v(-38.15, -17.65) * mm});
            skLineSegment(sketch, "E624", {"start": v(-38.15, -17.65) * mm, "end": v(-37.64, -17.58) * mm});
            skLineSegment(sketch, "E625", {"start": v(-37.64, -17.58) * mm, "end": v(-37.11, -17.53) * mm});
            skLineSegment(sketch, "E626", {"start": v(-37.11, -17.53) * mm, "end": v(-36.57, -17.5) * mm});
            skLineSegment(sketch, "E627", {"start": v(-36.57, -17.5) * mm, "end": v(-36.02, -17.48) * mm});
            skLineSegment(sketch, "E628", {"start": v(-36.02, -17.48) * mm, "end": v(-35.46, -17.48) * mm});
            skLineSegment(sketch, "E629", {"start": v(-35.46, -17.48) * mm, "end": v(-34.88, -17.48) * mm});
            skLineSegment(sketch, "E630", {"start": v(-34.88, -17.48) * mm, "end": v(-34.29, -17.5) * mm});
            skLineSegment(sketch, "E631", {"start": v(-34.29, -17.5) * mm, "end": v(-33.67, -17.5) * mm});
            skLineSegment(sketch, "E632", {"start": v(-33.67, -17.5) * mm, "end": v(-33.05, -17.51) * mm});
            skLineSegment(sketch, "E633", {"start": v(-33.05, -17.51) * mm, "end": v(-32.4, -17.51) * mm});
            skLineSegment(sketch, "E634", {"start": v(-32.4, -17.51) * mm, "end": v(-31.73, -17.5) * mm});
            skLineSegment(sketch, "E635", {"start": v(-31.73, -17.5) * mm, "end": v(-31.04, -17.48) * mm});
            skLineSegment(sketch, "E636", {"start": v(-31.04, -17.48) * mm, "end": v(-30.33, -17.44) * mm});
            skLineSegment(sketch, "E637", {"start": v(-30.33, -17.44) * mm, "end": v(-29.6, -17.38) * mm});
            skLineSegment(sketch, "E638", {"start": v(-29.6, -17.38) * mm, "end": v(-28.8, -17.3) * mm});
            skLineSegment(sketch, "E639", {"start": v(-28.8, -17.3) * mm, "end": v(-28, -17.2) * mm});
            skLineSegment(sketch, "E640", {"start": v(-28, -17.2) * mm, "end": v(-27.22, -17.08) * mm});
            skLineSegment(sketch, "E641", {"start": v(-27.22, -17.08) * mm, "end": v(-26.44, -16.92) * mm});
            skLineSegment(sketch, "E642", {"start": v(-26.44, -16.92) * mm, "end": v(-25.68, -16.74) * mm});
            skLineSegment(sketch, "E643", {"start": v(-25.68, -16.74) * mm, "end": v(-24.92, -16.54) * mm});
            skLineSegment(sketch, "E644", {"start": v(-24.92, -16.54) * mm, "end": v(-24.18, -16.3) * mm});
            skLineSegment(sketch, "E645", {"start": v(-24.18, -16.3) * mm, "end": v(-23.45, -16.05) * mm});
            skLineSegment(sketch, "E646", {"start": v(-23.45, -16.05) * mm, "end": v(-22.73, -15.77) * mm});
            skLineSegment(sketch, "E647", {"start": v(-22.73, -15.77) * mm, "end": v(-22.02, -15.47) * mm});
            skLineSegment(sketch, "E648", {"start": v(-22.02, -15.47) * mm, "end": v(-21.32, -15.14) * mm});
            skLineSegment(sketch, "E649", {"start": v(-21.32, -15.14) * mm, "end": v(-20.64, -14.8) * mm});
            skLineSegment(sketch, "E650", {"start": v(-20.64, -14.8) * mm, "end": v(-19.97, -14.42) * mm});
            skLineSegment(sketch, "E651", {"start": v(-19.97, -14.42) * mm, "end": v(-19.31, -14.03) * mm});
            skLineSegment(sketch, "E652", {"start": v(-19.31, -14.03) * mm, "end": v(-18.67, -13.62) * mm});
            skLineSegment(sketch, "E653", {"start": v(-18.67, -13.62) * mm, "end": v(-18.04, -13.18) * mm});
            skLineSegment(sketch, "E654", {"start": v(-18.04, -13.18) * mm, "end": v(-17.43, -12.73) * mm});
            skLineSegment(sketch, "E655", {"start": v(-17.43, -12.73) * mm, "end": v(-16.84, -12.25) * mm});
            skLineSegment(sketch, "E656", {"start": v(-16.84, -12.25) * mm, "end": v(-16.26, -11.76) * mm});
            skLineSegment(sketch, "E657", {"start": v(-16.26, -11.76) * mm, "end": v(-15.7, -11.24) * mm});
            skLineSegment(sketch, "E658", {"start": v(-15.7, -11.24) * mm, "end": v(-15.15, -10.71) * mm});
            skLineSegment(sketch, "E659", {"start": v(-15.15, -10.71) * mm, "end": v(-14.63, -10.16) * mm});
            skLineSegment(sketch, "E660", {"start": v(-14.63, -10.16) * mm, "end": v(-14.12, -9.6) * mm});
            skLineSegment(sketch, "E661", {"start": v(-14.12, -9.6) * mm, "end": v(-13.63, -9.02) * mm});
            skLineSegment(sketch, "E662", {"start": v(-13.63, -9.02) * mm, "end": v(-13.16, -8.42) * mm});
            skLineSegment(sketch, "E663", {"start": v(-13.16, -8.42) * mm, "end": v(-12.7, -7.8) * mm});
            skLineSegment(sketch, "E664", {"start": v(-12.7, -7.8) * mm, "end": v(-12.28, -7.17) * mm});
            skLineSegment(sketch, "E665", {"start": v(-12.28, -7.17) * mm, "end": v(-11.87, -6.53) * mm});
            skLineSegment(sketch, "E666", {"start": v(-11.87, -6.53) * mm, "end": v(-11.48, -5.87) * mm});
            skLineSegment(sketch, "E667", {"start": v(-11.48, -5.87) * mm, "end": v(-11.12, -5.2) * mm});
            skLineSegment(sketch, "E668", {"start": v(-11.12, -5.2) * mm, "end": v(-10.77, -4.5) * mm});
            skLineSegment(sketch, "E669", {"start": v(-10.77, -4.5) * mm, "end": v(-10.45, -3.8) * mm});
            skLineSegment(sketch, "E670", {"start": v(-10.45, -3.8) * mm, "end": v(-10.42, -3.73) * mm});
            skLineSegment(sketch, "E671", {"start": v(-10.42, -3.73) * mm, "end": v(-10.38, -3.65) * mm});
            skLineSegment(sketch, "E672", {"start": v(-10.38, -3.65) * mm, "end": v(-10.35, -3.57) * mm});
            skLineSegment(sketch, "E673", {"start": v(-10.35, -3.57) * mm, "end": v(-10.31, -3.49) * mm});
            skLineSegment(sketch, "E674", {"start": v(-10.31, -3.49) * mm, "end": v(-10.28, -3.4) * mm});
            skLineSegment(sketch, "E675", {"start": v(-10.28, -3.4) * mm, "end": v(-10.25, -3.33) * mm});
            skLineSegment(sketch, "E676", {"start": v(-10.25, -3.33) * mm, "end": v(-10.21, -3.24) * mm});
            skLineSegment(sketch, "E677", {"start": v(-10.21, -3.24) * mm, "end": v(-10.18, -3.16) * mm});
            skLineSegment(sketch, "E678", {"start": v(-10.18, -3.16) * mm, "end": v(-10.15, -3.08) * mm});
            skLineSegment(sketch, "E679", {"start": v(-10.15, -3.08) * mm, "end": v(-10.12, -3) * mm});
            skLineSegment(sketch, "E680", {"start": v(-10.12, -3) * mm, "end": v(-10.08, -2.91) * mm});
            skLineSegment(sketch, "E681", {"start": v(-10.08, -2.91) * mm, "end": v(-10.05, -2.83) * mm});
            skLineSegment(sketch, "E682", {"start": v(-10.05, -2.83) * mm, "end": v(-10.02, -2.75) * mm});
            skLineSegment(sketch, "E683", {"start": v(-10.02, -2.75) * mm, "end": v(-9.99, -2.66) * mm});
            skLineSegment(sketch, "E684", {"start": v(-9.99, -2.66) * mm, "end": v(-9.96, -2.58) * mm});
            skLineSegment(sketch, "E685", {"start": v(-9.96, -2.58) * mm, "end": v(-9.93, -2.5) * mm});
            skLineSegment(sketch, "E686", {"start": v(-9.93, -2.5) * mm, "end": v(-9.9, -2.41) * mm});
            skLineSegment(sketch, "E687", {"start": v(-9.9, -2.41) * mm, "end": v(-9.87, -2.33) * mm});
            skLineSegment(sketch, "E688", {"start": v(-9.87, -2.33) * mm, "end": v(-9.84, -2.24) * mm});
            skLineSegment(sketch, "E689", {"start": v(-9.84, -2.24) * mm, "end": v(-9.8, -2.16) * mm});
            skLineSegment(sketch, "E690", {"start": v(-9.8, -2.16) * mm, "end": v(-9.78, -2.08) * mm});
            skLineSegment(sketch, "E691", {"start": v(-9.78, -2.08) * mm, "end": v(-9.75, -2) * mm});
            skLineSegment(sketch, "E692", {"start": v(-9.75, -2) * mm, "end": v(-9.72, -1.9) * mm});
            skLineSegment(sketch, "E693", {"start": v(-9.72, -1.9) * mm, "end": v(-9.7, -1.82) * mm});
            skLineSegment(sketch, "E694", {"start": v(-9.7, -1.82) * mm, "end": v(-9.66, -1.74) * mm});
            skLineSegment(sketch, "E695", {"start": v(-9.66, -1.74) * mm, "end": v(-9.64, -1.65) * mm});
            skLineSegment(sketch, "E696", {"start": v(-9.64, -1.65) * mm, "end": v(-9.6, -1.57) * mm});
            skLineSegment(sketch, "E697", {"start": v(-9.6, -1.57) * mm, "end": v(-9.58, -1.49) * mm});
            skLineSegment(sketch, "E698", {"start": v(-9.58, -1.49) * mm, "end": v(-9.56, -1.4) * mm});
            skLineSegment(sketch, "E699", {"start": v(-9.56, -1.4) * mm, "end": v(-9.53, -1.32) * mm});
            skLineSegment(sketch, "E700", {"start": v(-9.53, -1.32) * mm, "end": v(-9.5, -1.23) * mm});
            skLineSegment(sketch, "E701", {"start": v(-9.5, -1.23) * mm, "end": v(-9.48, -1.15) * mm});
            skLineSegment(sketch, "E702", {"start": v(-9.48, -1.15) * mm, "end": v(-9.31, -0.66) * mm});
            skLineSegment(sketch, "E703", {"start": v(-9.31, -0.66) * mm, "end": v(-9.15, -0.18) * mm});
            skLineSegment(sketch, "E704", {"start": v(-9.15, -0.18) * mm, "end": v(-8.98, 0.3) * mm});
            skLineSegment(sketch, "E705", {"start": v(-8.98, 0.3) * mm, "end": v(-8.82, 0.77) * mm});
            skLineSegment(sketch, "E706", {"start": v(-8.82, 0.77) * mm, "end": v(-8.65, 1.23) * mm});
            skLineSegment(sketch, "E707", {"start": v(-8.65, 1.23) * mm, "end": v(-8.48, 1.69) * mm});
            skLineSegment(sketch, "E708", {"start": v(-8.48, 1.69) * mm, "end": v(-8.3, 2.14) * mm});
            skLineSegment(sketch, "E709", {"start": v(-8.3, 2.14) * mm, "end": v(-8.13, 2.57) * mm});
            skLineSegment(sketch, "E710", {"start": v(-8.13, 2.57) * mm, "end": v(-7.94, 3) * mm});
            skLineSegment(sketch, "E711", {"start": v(-7.94, 3) * mm, "end": v(-7.75, 3.42) * mm});
            skLineSegment(sketch, "E712", {"start": v(-7.75, 3.42) * mm, "end": v(-7.54, 3.82) * mm});
            skLineSegment(sketch, "E713", {"start": v(-7.54, 3.82) * mm, "end": v(-7.33, 4.22) * mm});
            skLineSegment(sketch, "E714", {"start": v(-7.33, 4.22) * mm, "end": v(-7.1, 4.6) * mm});
            skLineSegment(sketch, "E715", {"start": v(-7.1, 4.6) * mm, "end": v(-6.87, 4.97) * mm});
            skLineSegment(sketch, "E716", {"start": v(-6.87, 4.97) * mm, "end": v(-6.62, 5.32) * mm});
            skLineSegment(sketch, "E717", {"start": v(-6.62, 5.32) * mm, "end": v(-6.35, 5.66) * mm});
            skLineSegment(sketch, "E718", {"start": v(-6.35, 5.66) * mm, "end": v(-6.07, 5.98) * mm});
            skLineSegment(sketch, "E719", {"start": v(-6.07, 5.98) * mm, "end": v(-5.77, 6.3) * mm});
            skLineSegment(sketch, "E720", {"start": v(-5.77, 6.3) * mm, "end": v(-5.45, 6.58) * mm});
            skLineSegment(sketch, "E721", {"start": v(-5.45, 6.58) * mm, "end": v(-5.11, 6.86) * mm});
            skLineSegment(sketch, "E722", {"start": v(-5.11, 6.86) * mm, "end": v(-4.76, 7.11) * mm});
            skLineSegment(sketch, "E723", {"start": v(-4.76, 7.11) * mm, "end": v(-4.38, 7.35) * mm});
            skLineSegment(sketch, "E724", {"start": v(-4.38, 7.35) * mm, "end": v(-3.97, 7.57) * mm});
            skLineSegment(sketch, "E725", {"start": v(-3.97, 7.57) * mm, "end": v(-3.54, 7.76) * mm});
            skLineSegment(sketch, "E726", {"start": v(-3.54, 7.76) * mm, "end": v(-3.1, 7.94) * mm});
            skLineSegment(sketch, "E727", {"start": v(-3.1, 7.94) * mm, "end": v(-2.6, 8.1) * mm});
            skLineSegment(sketch, "E728", {"start": v(-2.6, 8.1) * mm, "end": v(-2.1, 8.23) * mm});
            skLineSegment(sketch, "E729", {"start": v(-2.1, 8.23) * mm, "end": v(-1.56, 8.34) * mm});
            skLineSegment(sketch, "E730", {"start": v(-1.56, 8.34) * mm, "end": v(-1, 8.43) * mm});
            skLineSegment(sketch, "E731", {"start": v(-1, 8.43) * mm, "end": v(-0.4, 8.49) * mm});
            skLineSegment(sketch, "E732", {"start": v(-0.4, 8.49) * mm, "end": v(0.24, 8.53) * mm});
            skLineSegment(sketch, "E733", {"start": v(0.24, 8.53) * mm, "end": v(0.9, 8.54) * mm});
            skLineSegment(sketch, "E734", {"start": v(0.9, 8.54) * mm, "end": v(1.57, 8.53) * mm});
            skLineSegment(sketch, "E735", {"start": v(1.57, 8.53) * mm, "end": v(2.2, 8.49) * mm});
            skLineSegment(sketch, "E736", {"start": v(2.2, 8.49) * mm, "end": v(2.8, 8.43) * mm});
            skLineSegment(sketch, "E737", {"start": v(2.8, 8.43) * mm, "end": v(3.37, 8.34) * mm});
            skLineSegment(sketch, "E738", {"start": v(3.37, 8.34) * mm, "end": v(3.91, 8.23) * mm});
            skLineSegment(sketch, "E739", {"start": v(3.91, 8.23) * mm, "end": v(4.42, 8.1) * mm});
            skLineSegment(sketch, "E740", {"start": v(4.42, 8.1) * mm, "end": v(4.9, 7.94) * mm});
            skLineSegment(sketch, "E741", {"start": v(4.9, 7.94) * mm, "end": v(5.36, 7.76) * mm});
            skLineSegment(sketch, "E742", {"start": v(5.36, 7.76) * mm, "end": v(5.78, 7.57) * mm});
            skLineSegment(sketch, "E743", {"start": v(5.78, 7.57) * mm, "end": v(6.19, 7.35) * mm});
            skLineSegment(sketch, "E744", {"start": v(6.19, 7.35) * mm, "end": v(6.57, 7.11) * mm});
            skLineSegment(sketch, "E745", {"start": v(6.57, 7.11) * mm, "end": v(6.93, 6.86) * mm});
            skLineSegment(sketch, "E746", {"start": v(6.93, 6.86) * mm, "end": v(7.26, 6.58) * mm});
            skLineSegment(sketch, "E747", {"start": v(7.26, 6.58) * mm, "end": v(7.58, 6.3) * mm});
            skLineSegment(sketch, "E748", {"start": v(7.58, 6.3) * mm, "end": v(7.88, 5.98) * mm});
            skLineSegment(sketch, "E749", {"start": v(7.88, 5.98) * mm, "end": v(8.16, 5.66) * mm});
            skLineSegment(sketch, "E750", {"start": v(8.16, 5.66) * mm, "end": v(8.43, 5.32) * mm});
            skLineSegment(sketch, "E751", {"start": v(8.43, 5.32) * mm, "end": v(8.68, 4.97) * mm});
            skLineSegment(sketch, "E752", {"start": v(8.68, 4.97) * mm, "end": v(8.92, 4.6) * mm});
            skLineSegment(sketch, "E753", {"start": v(8.92, 4.6) * mm, "end": v(9.14, 4.22) * mm});
            skLineSegment(sketch, "E754", {"start": v(9.14, 4.22) * mm, "end": v(9.35, 3.82) * mm});
            skLineSegment(sketch, "E755", {"start": v(9.35, 3.82) * mm, "end": v(9.56, 3.42) * mm});
            skLineSegment(sketch, "E756", {"start": v(9.56, 3.42) * mm, "end": v(9.75, 3) * mm});
            skLineSegment(sketch, "E757", {"start": v(9.75, 3) * mm, "end": v(9.94, 2.57) * mm});
            skLineSegment(sketch, "E758", {"start": v(9.94, 2.57) * mm, "end": v(10.12, 2.14) * mm});
            skLineSegment(sketch, "E759", {"start": v(10.12, 2.14) * mm, "end": v(10.3, 1.69) * mm});
            skLineSegment(sketch, "E760", {"start": v(10.3, 1.69) * mm, "end": v(10.46, 1.23) * mm});
            skLineSegment(sketch, "E761", {"start": v(10.46, 1.23) * mm, "end": v(10.63, 0.77) * mm});
            skLineSegment(sketch, "E762", {"start": v(10.63, 0.77) * mm, "end": v(10.8, 0.3) * mm});
            skLineSegment(sketch, "E763", {"start": v(10.8, 0.3) * mm, "end": v(10.96, -0.18) * mm});
            skLineSegment(sketch, "E764", {"start": v(10.96, -0.18) * mm, "end": v(11.12, -0.66) * mm});
            skLineSegment(sketch, "E765", {"start": v(11.12, -0.66) * mm, "end": v(11.3, -1.15) * mm});
            skLineSegment(sketch, "E766", {"start": v(11.3, -1.15) * mm, "end": v(11.32, -1.23) * mm});
            skLineSegment(sketch, "E767", {"start": v(11.32, -1.23) * mm, "end": v(11.34, -1.32) * mm});
            skLineSegment(sketch, "E768", {"start": v(11.34, -1.32) * mm, "end": v(11.37, -1.4) * mm});
            skLineSegment(sketch, "E769", {"start": v(11.37, -1.4) * mm, "end": v(11.4, -1.49) * mm});
            skLineSegment(sketch, "E770", {"start": v(11.4, -1.49) * mm, "end": v(11.42, -1.57) * mm});
            skLineSegment(sketch, "E771", {"start": v(11.42, -1.57) * mm, "end": v(11.45, -1.65) * mm});
            skLineSegment(sketch, "E772", {"start": v(11.45, -1.65) * mm, "end": v(11.48, -1.74) * mm});
            skLineSegment(sketch, "E773", {"start": v(11.48, -1.74) * mm, "end": v(11.5, -1.82) * mm});
            skLineSegment(sketch, "E774", {"start": v(11.5, -1.82) * mm, "end": v(11.53, -1.9) * mm});
            skLineSegment(sketch, "E775", {"start": v(11.53, -1.9) * mm, "end": v(11.56, -2) * mm});
            skLineSegment(sketch, "E776", {"start": v(11.56, -2) * mm, "end": v(11.59, -2.08) * mm});
            skLineSegment(sketch, "E777", {"start": v(11.59, -2.08) * mm, "end": v(11.62, -2.16) * mm});
            skLineSegment(sketch, "E778", {"start": v(11.62, -2.16) * mm, "end": v(11.65, -2.24) * mm});
            skLineSegment(sketch, "E779", {"start": v(11.65, -2.24) * mm, "end": v(11.68, -2.33) * mm});
            skLineSegment(sketch, "E780", {"start": v(11.68, -2.33) * mm, "end": v(11.7, -2.41) * mm});
            skLineSegment(sketch, "E781", {"start": v(11.7, -2.41) * mm, "end": v(11.74, -2.5) * mm});
            skLineSegment(sketch, "E782", {"start": v(11.74, -2.5) * mm, "end": v(11.77, -2.58) * mm});
            skLineSegment(sketch, "E783", {"start": v(11.77, -2.58) * mm, "end": v(11.8, -2.66) * mm});
            skLineSegment(sketch, "E784", {"start": v(11.8, -2.66) * mm, "end": v(11.83, -2.75) * mm});
            skLineSegment(sketch, "E785", {"start": v(11.83, -2.75) * mm, "end": v(11.86, -2.83) * mm});
            skLineSegment(sketch, "E786", {"start": v(11.86, -2.83) * mm, "end": v(11.9, -2.91) * mm});
            skLineSegment(sketch, "E787", {"start": v(11.9, -2.91) * mm, "end": v(11.93, -3) * mm});
            skLineSegment(sketch, "E788", {"start": v(11.93, -3) * mm, "end": v(11.96, -3.08) * mm});
            skLineSegment(sketch, "E789", {"start": v(11.96, -3.08) * mm, "end": v(12, -3.16) * mm});
            skLineSegment(sketch, "E790", {"start": v(12, -3.16) * mm, "end": v(12.03, -3.24) * mm});
            skLineSegment(sketch, "E791", {"start": v(12.03, -3.24) * mm, "end": v(12.06, -3.33) * mm});
            skLineSegment(sketch, "E792", {"start": v(12.06, -3.33) * mm, "end": v(12.1, -3.4) * mm});
            skLineSegment(sketch, "E793", {"start": v(12.1, -3.4) * mm, "end": v(12.13, -3.49) * mm});
            skLineSegment(sketch, "E794", {"start": v(12.13, -3.49) * mm, "end": v(12.16, -3.57) * mm});
            skLineSegment(sketch, "E795", {"start": v(12.16, -3.57) * mm, "end": v(12.2, -3.65) * mm});
            skLineSegment(sketch, "E796", {"start": v(12.2, -3.65) * mm, "end": v(12.23, -3.73) * mm});
            skLineSegment(sketch, "E797", {"start": v(12.23, -3.73) * mm, "end": v(12.26, -3.8) * mm});
            skLineSegment(sketch, "E798", {"start": v(12.26, -3.8) * mm, "end": v(12.6, -4.55) * mm});
            skLineSegment(sketch, "E799", {"start": v(12.6, -4.55) * mm, "end": v(12.97, -5.28) * mm});
            skLineSegment(sketch, "E800", {"start": v(12.97, -5.28) * mm, "end": v(13.37, -6) * mm});
            skLineSegment(sketch, "E801", {"start": v(13.37, -6) * mm, "end": v(13.79, -6.7) * mm});
            skLineSegment(sketch, "E802", {"start": v(13.79, -6.7) * mm, "end": v(14.23, -7.38) * mm});
            skLineSegment(sketch, "E803", {"start": v(14.23, -7.38) * mm, "end": v(14.7, -8.04) * mm});
            skLineSegment(sketch, "E804", {"start": v(14.7, -8.04) * mm, "end": v(15.18, -8.7) * mm});
            skLineSegment(sketch, "E805", {"start": v(15.18, -8.7) * mm, "end": v(15.7, -9.32) * mm});
            skLineSegment(sketch, "E806", {"start": v(15.7, -9.32) * mm, "end": v(16.23, -9.93) * mm});
            skLineSegment(sketch, "E807", {"start": v(16.23, -9.93) * mm, "end": v(16.78, -10.52) * mm});
            skLineSegment(sketch, "E808", {"start": v(16.78, -10.52) * mm, "end": v(17.35, -11.1) * mm});
            skLineSegment(sketch, "E809", {"start": v(17.35, -11.1) * mm, "end": v(17.95, -11.65) * mm});
            skLineSegment(sketch, "E810", {"start": v(17.95, -11.65) * mm, "end": v(18.56, -12.18) * mm});
            skLineSegment(sketch, "E811", {"start": v(18.56, -12.18) * mm, "end": v(19.2, -12.68) * mm});
            skLineSegment(sketch, "E812", {"start": v(19.2, -12.68) * mm, "end": v(19.84, -13.17) * mm});
            skLineSegment(sketch, "E813", {"start": v(19.84, -13.17) * mm, "end": v(20.5, -13.63) * mm});
            skLineSegment(sketch, "E814", {"start": v(20.5, -13.63) * mm, "end": v(21.2, -14.07) * mm});
            skLineSegment(sketch, "E815", {"start": v(21.2, -14.07) * mm, "end": v(21.9, -14.49) * mm});
            skLineSegment(sketch, "E816", {"start": v(21.9, -14.49) * mm, "end": v(22.6, -14.88) * mm});
            skLineSegment(sketch, "E817", {"start": v(22.6, -14.88) * mm, "end": v(23.34, -15.24) * mm});
            skLineSegment(sketch, "E818", {"start": v(23.34, -15.24) * mm, "end": v(24.09, -15.58) * mm});
            skLineSegment(sketch, "E819", {"start": v(24.09, -15.58) * mm, "end": v(24.85, -15.9) * mm});
            skLineSegment(sketch, "E820", {"start": v(24.85, -15.9) * mm, "end": v(25.62, -16.18) * mm});
            skLineSegment(sketch, "E821", {"start": v(25.62, -16.18) * mm, "end": v(26.4, -16.44) * mm});
            skLineSegment(sketch, "E822", {"start": v(26.4, -16.44) * mm, "end": v(27.2, -16.67) * mm});
            skLineSegment(sketch, "E823", {"start": v(27.2, -16.67) * mm, "end": v(28.02, -16.87) * mm});
            skLineSegment(sketch, "E824", {"start": v(28.02, -16.87) * mm, "end": v(28.84, -17.04) * mm});
            skLineSegment(sketch, "E825", {"start": v(28.84, -17.04) * mm, "end": v(29.67, -17.19) * mm});
            skLineSegment(sketch, "E826", {"start": v(29.67, -17.19) * mm, "end": v(30.51, -17.3) * mm});
            skLineSegment(sketch, "E827", {"start": v(30.51, -17.3) * mm, "end": v(31.36, -17.38) * mm});
            skLineSegment(sketch, "E828", {"start": v(31.36, -17.38) * mm, "end": v(32.22, -17.43) * mm});
            skLineSegment(sketch, "E829", {"start": v(32.22, -17.43) * mm, "end": v(33.1, -17.44) * mm});
            skLineSegment(sketch, "E830", {"start": v(33.1, -17.44) * mm, "end": v(33.89, -17.43) * mm});
            skLineSegment(sketch, "E831", {"start": v(33.89, -17.43) * mm, "end": v(34.68, -17.39) * mm});
            skLineSegment(sketch, "E832", {"start": v(34.68, -17.39) * mm, "end": v(35.47, -17.32) * mm});
            skLineSegment(sketch, "E833", {"start": v(35.47, -17.32) * mm, "end": v(36.24, -17.23) * mm});
            skLineSegment(sketch, "E834", {"start": v(36.24, -17.23) * mm, "end": v(37.01, -17.1) * mm});
            skLineSegment(sketch, "E835", {"start": v(37.01, -17.1) * mm, "end": v(37.77, -16.96) * mm});
            skLineSegment(sketch, "E836", {"start": v(37.77, -16.96) * mm, "end": v(38.52, -16.79) * mm});
            skLineSegment(sketch, "E837", {"start": v(38.52, -16.79) * mm, "end": v(39.26, -16.6) * mm});
            skLineSegment(sketch, "E838", {"start": v(39.26, -16.6) * mm, "end": v(40, -16.37) * mm});
            skLineSegment(sketch, "E839", {"start": v(40, -16.37) * mm, "end": v(40.71, -16.13) * mm});
            skLineSegment(sketch, "E840", {"start": v(40.71, -16.13) * mm, "end": v(41.42, -15.86) * mm});
            skLineSegment(sketch, "E841", {"start": v(41.42, -15.86) * mm, "end": v(42.12, -15.57) * mm});
            skLineSegment(sketch, "E842", {"start": v(42.12, -15.57) * mm, "end": v(42.8, -15.26) * mm});
            skLineSegment(sketch, "E843", {"start": v(42.8, -15.26) * mm, "end": v(43.48, -14.93) * mm});
            skLineSegment(sketch, "E844", {"start": v(43.48, -14.93) * mm, "end": v(44.14, -14.57) * mm});
            skLineSegment(sketch, "E845", {"start": v(44.14, -14.57) * mm, "end": v(44.8, -14.2) * mm});
            skLineSegment(sketch, "E846", {"start": v(44.8, -14.2) * mm, "end": v(45.42, -13.8) * mm});
            skLineSegment(sketch, "E847", {"start": v(45.42, -13.8) * mm, "end": v(46.04, -13.39) * mm});
            skLineSegment(sketch, "E848", {"start": v(46.04, -13.39) * mm, "end": v(46.65, -12.95) * mm});
            skLineSegment(sketch, "E849", {"start": v(46.65, -12.95) * mm, "end": v(47.24, -12.5) * mm});
            skLineSegment(sketch, "E850", {"start": v(47.24, -12.5) * mm, "end": v(47.82, -12.02) * mm});
            skLineSegment(sketch, "E851", {"start": v(47.82, -12.02) * mm, "end": v(48.37, -11.53) * mm});
            skLineSegment(sketch, "E852", {"start": v(48.37, -11.53) * mm, "end": v(48.92, -11.02) * mm});
            skLineSegment(sketch, "E853", {"start": v(48.92, -11.02) * mm, "end": v(49.44, -10.5) * mm});
            skLineSegment(sketch, "E854", {"start": v(49.44, -10.5) * mm, "end": v(49.95, -9.95) * mm});
            skLineSegment(sketch, "E855", {"start": v(49.95, -9.95) * mm, "end": v(50.44, -9.39) * mm});
            skLineSegment(sketch, "E856", {"start": v(50.44, -9.39) * mm, "end": v(50.91, -8.8) * mm});
            skLineSegment(sketch, "E857", {"start": v(50.91, -8.8) * mm, "end": v(51.37, -8.22) * mm});
            skLineSegment(sketch, "E858", {"start": v(51.37, -8.22) * mm, "end": v(51.8, -7.61) * mm});
            skLineSegment(sketch, "E859", {"start": v(51.8, -7.61) * mm, "end": v(52.22, -6.99) * mm});
            skLineSegment(sketch, "E860", {"start": v(52.22, -6.99) * mm, "end": v(52.61, -6.35) * mm});
            skLineSegment(sketch, "E861", {"start": v(52.61, -6.35) * mm, "end": v(52.99, -5.7) * mm});
            skLineSegment(sketch, "E862", {"start": v(52.99, -5.7) * mm, "end": v(53.36, -5.04) * mm});
            skLineSegment(sketch, "E863", {"start": v(53.36, -5.04) * mm, "end": v(53.7, -4.39) * mm});
            skLineSegment(sketch, "E864", {"start": v(53.7, -4.39) * mm, "end": v(54.01, -3.75) * mm});
            skLineSegment(sketch, "E865", {"start": v(54.01, -3.75) * mm, "end": v(54.3, -3.12) * mm});
            skLineSegment(sketch, "E866", {"start": v(54.3, -3.12) * mm, "end": v(54.57, -2.51) * mm});
            skLineSegment(sketch, "E867", {"start": v(54.57, -2.51) * mm, "end": v(54.83, -1.92) * mm});
            skLineSegment(sketch, "E868", {"start": v(54.83, -1.92) * mm, "end": v(55.07, -1.34) * mm});
            skLineSegment(sketch, "E869", {"start": v(55.07, -1.34) * mm, "end": v(55.3, -0.78) * mm});
            skLineSegment(sketch, "E870", {"start": v(55.3, -0.78) * mm, "end": v(55.54, -0.23) * mm});
            skLineSegment(sketch, "E871", {"start": v(55.54, -0.23) * mm, "end": v(55.77, 0.3) * mm});
            skLineSegment(sketch, "E872", {"start": v(55.77, 0.3) * mm, "end": v(56, 0.81) * mm});
            skLineSegment(sketch, "E873", {"start": v(56, 0.81) * mm, "end": v(56.25, 1.3) * mm});
            skLineSegment(sketch, "E874", {"start": v(56.25, 1.3) * mm, "end": v(56.5, 1.78) * mm});
            skLineSegment(sketch, "E875", {"start": v(56.5, 1.78) * mm, "end": v(56.78, 2.23) * mm});
            skLineSegment(sketch, "E876", {"start": v(56.78, 2.23) * mm, "end": v(57.07, 2.67) * mm});
            skLineSegment(sketch, "E877", {"start": v(57.07, 2.67) * mm, "end": v(57.39, 3.08) * mm});
            skLineSegment(sketch, "E878", {"start": v(57.39, 3.08) * mm, "end": v(57.73, 3.48) * mm});
            skLineSegment(sketch, "E879", {"start": v(57.73, 3.48) * mm, "end": v(58.1, 3.85) * mm});
            skLineSegment(sketch, "E880", {"start": v(58.1, 3.85) * mm, "end": v(58.51, 4.2) * mm});
            skLineSegment(sketch, "E881", {"start": v(58.51, 4.2) * mm, "end": v(58.96, 4.53) * mm});
            skLineSegment(sketch, "E882", {"start": v(58.96, 4.53) * mm, "end": v(59.45, 4.83) * mm});
            skLineSegment(sketch, "E883", {"start": v(59.45, 4.83) * mm, "end": v(60, 5.11) * mm});
            skLineSegment(sketch, "E884", {"start": v(60, 5.11) * mm, "end": v(60.58, 5.37) * mm});
            skLineSegment(sketch, "E885", {"start": v(60.58, 5.37) * mm, "end": v(61.23, 5.6) * mm});
            skLineSegment(sketch, "E886", {"start": v(61.23, 5.6) * mm, "end": v(61.93, 5.8) * mm});
            skLineSegment(sketch, "E887", {"start": v(61.93, 5.8) * mm, "end": v(62.7, 5.99) * mm});
            skLineSegment(sketch, "E888", {"start": v(62.7, 5.99) * mm, "end": v(63.53, 6.14) * mm});
            skLineSegment(sketch, "E889", {"start": v(63.53, 6.14) * mm, "end": v(64.43, 6.27) * mm});
            skLineSegment(sketch, "E890", {"start": v(64.43, 6.27) * mm, "end": v(65.4, 6.37) * mm});
            skLineSegment(sketch, "E891", {"start": v(65.4, 6.37) * mm, "end": v(66.46, 6.44) * mm});
            skLineSegment(sketch, "E892", {"start": v(66.46, 6.44) * mm, "end": v(67.6, 6.49) * mm});
            skLineSegment(sketch, "E893", {"start": v(67.6, 6.49) * mm, "end": v(68.82, 6.5) * mm});
            skLineSegment(sketch, "E894", {"start": v(68.82, 6.5) * mm, "end": v(68.82, 6.71) * mm});
            skLineSegment(sketch, "E895", {"start": v(68.82, 6.71) * mm, "end": v(68.82, 6.9) * mm});
            skLineSegment(sketch, "E896", {"start": v(68.82, 6.9) * mm, "end": v(68.82, 7.08) * mm});
            skLineSegment(sketch, "E897", {"start": v(68.82, 7.08) * mm, "end": v(68.82, 7.24) * mm});
            skLineSegment(sketch, "E898", {"start": v(68.82, 7.24) * mm, "end": v(68.82, 7.38) * mm});
            skLineSegment(sketch, "E899", {"start": v(68.82, 7.38) * mm, "end": v(68.82, 7.51) * mm});
            skLineSegment(sketch, "E900", {"start": v(68.82, 7.51) * mm, "end": v(68.82, 7.63) * mm});
            skLineSegment(sketch, "E901", {"start": v(68.82, 7.63) * mm, "end": v(68.82, 7.74) * mm});
            skLineSegment(sketch, "E902", {"start": v(68.82, 7.74) * mm, "end": v(68.82, 7.84) * mm});
            skLineSegment(sketch, "E903", {"start": v(68.82, 7.84) * mm, "end": v(68.82, 7.93) * mm});
            skLineSegment(sketch, "E904", {"start": v(68.82, 7.93) * mm, "end": v(68.82, 8) * mm});
            skLineSegment(sketch, "E905", {"start": v(68.82, 8) * mm, "end": v(68.82, 8.08) * mm});
            skLineSegment(sketch, "E906", {"start": v(68.82, 8.08) * mm, "end": v(68.82, 8.15) * mm});
            skLineSegment(sketch, "E907", {"start": v(68.82, 8.15) * mm, "end": v(68.82, 8.22) * mm});
            skLineSegment(sketch, "E908", {"start": v(68.82, 8.22) * mm, "end": v(68.82, 8.28) * mm});
            skLineSegment(sketch, "E909", {"start": v(68.82, 8.28) * mm, "end": v(68.82, 8.34) * mm});
            skLineSegment(sketch, "E910", {"start": v(68.82, 8.34) * mm, "end": v(68.82, 8.4) * mm});
            skLineSegment(sketch, "E911", {"start": v(68.82, 8.4) * mm, "end": v(68.82, 8.47) * mm});
            skLineSegment(sketch, "E912", {"start": v(68.82, 8.47) * mm, "end": v(68.82, 8.53) * mm});
            skLineSegment(sketch, "E913", {"start": v(68.82, 8.53) * mm, "end": v(68.82, 8.6) * mm});
            skLineSegment(sketch, "E914", {"start": v(68.82, 8.6) * mm, "end": v(68.82, 8.68) * mm});
            skLineSegment(sketch, "E915", {"start": v(68.82, 8.68) * mm, "end": v(68.82, 8.75) * mm});
            skLineSegment(sketch, "E916", {"start": v(68.82, 8.75) * mm, "end": v(68.82, 8.84) * mm});
            skLineSegment(sketch, "E917", {"start": v(68.82, 8.84) * mm, "end": v(68.82, 8.93) * mm});
            skLineSegment(sketch, "E918", {"start": v(68.82, 8.93) * mm, "end": v(68.82, 9.04) * mm});
            skLineSegment(sketch, "E919", {"start": v(68.82, 9.04) * mm, "end": v(68.82, 9.15) * mm});
            skLineSegment(sketch, "E920", {"start": v(68.82, 9.15) * mm, "end": v(68.82, 9.28) * mm});
            skLineSegment(sketch, "E921", {"start": v(68.82, 9.28) * mm, "end": v(68.82, 9.42) * mm});
            skLineSegment(sketch, "E922", {"start": v(68.82, 9.42) * mm, "end": v(68.82, 9.57) * mm});
            skLineSegment(sketch, "E923", {"start": v(68.82, 9.57) * mm, "end": v(68.82, 9.74) * mm});
            skLineSegment(sketch, "E924", {"start": v(68.82, 9.74) * mm, "end": v(68.82, 9.92) * mm});
            skLineSegment(sketch, "E925", {"start": v(68.82, 9.92) * mm, "end": v(68.82, 10.13) * mm});
            skLineSegment(sketch, "E926", {"start": v(68.82, 10.13) * mm, "end": v(68.25, 10.13) * mm});
            skLineSegment(sketch, "E927", {"start": v(-12.39, 4.32) * mm, "end": v(-12.46, 3.36) * mm});
            skLineSegment(sketch, "E928", {"start": v(-12.46, 3.36) * mm, "end": v(-12.58, 2.41) * mm});
            skLineSegment(sketch, "E929", {"start": v(-12.58, 2.41) * mm, "end": v(-12.75, 1.48) * mm});
            skLineSegment(sketch, "E930", {"start": v(-12.75, 1.48) * mm, "end": v(-12.96, 0.57) * mm});
            skLineSegment(sketch, "E931", {"start": v(-12.96, 0.57) * mm, "end": v(-13.21, -0.33) * mm});
            skLineSegment(sketch, "E932", {"start": v(-13.21, -0.33) * mm, "end": v(-13.51, -1.2) * mm});
            skLineSegment(sketch, "E933", {"start": v(-13.51, -1.2) * mm, "end": v(-13.85, -2.07) * mm});
            skLineSegment(sketch, "E934", {"start": v(-13.85, -2.07) * mm, "end": v(-14.23, -2.9) * mm});
            skLineSegment(sketch, "E935", {"start": v(-14.23, -2.9) * mm, "end": v(-14.65, -3.72) * mm});
            skLineSegment(sketch, "E936", {"start": v(-14.65, -3.72) * mm, "end": v(-15.1, -4.51) * mm});
            skLineSegment(sketch, "E937", {"start": v(-15.1, -4.51) * mm, "end": v(-15.6, -5.28) * mm});
            skLineSegment(sketch, "E938", {"start": v(-15.6, -5.28) * mm, "end": v(-16.12, -6.02) * mm});
            skLineSegment(sketch, "E939", {"start": v(-16.12, -6.02) * mm, "end": v(-16.69, -6.74) * mm});
            skLineSegment(sketch, "E940", {"start": v(-16.69, -6.74) * mm, "end": v(-17.28, -7.42) * mm});
            skLineSegment(sketch, "E941", {"start": v(-17.28, -7.42) * mm, "end": v(-17.9, -8.08) * mm});
            skLineSegment(sketch, "E942", {"start": v(-17.9, -8.08) * mm, "end": v(-18.57, -8.7) * mm});
            skLineSegment(sketch, "E943", {"start": v(-18.57, -8.7) * mm, "end": v(-19.25, -9.3) * mm});
            skLineSegment(sketch, "E944", {"start": v(-19.25, -9.3) * mm, "end": v(-19.97, -9.86) * mm});
            skLineSegment(sketch, "E945", {"start": v(-19.97, -9.86) * mm, "end": v(-20.7, -10.4) * mm});
            skLineSegment(sketch, "E946", {"start": v(-20.7, -10.4) * mm, "end": v(-21.48, -10.88) * mm});
            skLineSegment(sketch, "E947", {"start": v(-21.48, -10.88) * mm, "end": v(-22.27, -11.34) * mm});
            skLineSegment(sketch, "E948", {"start": v(-22.27, -11.34) * mm, "end": v(-23.09, -11.76) * mm});
            skLineSegment(sketch, "E949", {"start": v(-23.09, -11.76) * mm, "end": v(-23.92, -12.14) * mm});
            skLineSegment(sketch, "E950", {"start": v(-23.92, -12.14) * mm, "end": v(-24.78, -12.48) * mm});
            skLineSegment(sketch, "E951", {"start": v(-24.78, -12.48) * mm, "end": v(-25.66, -12.78) * mm});
            skLineSegment(sketch, "E952", {"start": v(-25.66, -12.78) * mm, "end": v(-26.56, -13.03) * mm});
            skLineSegment(sketch, "E953", {"start": v(-26.56, -13.03) * mm, "end": v(-27.47, -13.24) * mm});
            skLineSegment(sketch, "E954", {"start": v(-27.47, -13.24) * mm, "end": v(-28.4, -13.4) * mm});
            skLineSegment(sketch, "E955", {"start": v(-28.4, -13.4) * mm, "end": v(-29.35, -13.53) * mm});
            skLineSegment(sketch, "E956", {"start": v(-29.35, -13.53) * mm, "end": v(-30.3, -13.6) * mm});
            skLineSegment(sketch, "E957", {"start": v(-30.3, -13.6) * mm, "end": v(-31.28, -13.63) * mm});
            skLineSegment(sketch, "E958", {"start": v(-31.28, -13.63) * mm, "end": v(-32.25, -13.6) * mm});
            skLineSegment(sketch, "E959", {"start": v(-32.25, -13.6) * mm, "end": v(-33.21, -13.53) * mm});
            skLineSegment(sketch, "E960", {"start": v(-33.21, -13.53) * mm, "end": v(-34.16, -13.4) * mm});
            skLineSegment(sketch, "E961", {"start": v(-34.16, -13.4) * mm, "end": v(-35.09, -13.24) * mm});
            skLineSegment(sketch, "E962", {"start": v(-35.09, -13.24) * mm, "end": v(-36, -13.03) * mm});
            skLineSegment(sketch, "E963", {"start": v(-36, -13.03) * mm, "end": v(-36.9, -12.78) * mm});
            skLineSegment(sketch, "E964", {"start": v(-36.9, -12.78) * mm, "end": v(-37.78, -12.48) * mm});
            skLineSegment(sketch, "E965", {"start": v(-37.78, -12.48) * mm, "end": v(-38.64, -12.14) * mm});
            skLineSegment(sketch, "E966", {"start": v(-38.64, -12.14) * mm, "end": v(-39.47, -11.76) * mm});
            skLineSegment(sketch, "E967", {"start": v(-39.47, -11.76) * mm, "end": v(-40.29, -11.34) * mm});
            skLineSegment(sketch, "E968", {"start": v(-40.29, -11.34) * mm, "end": v(-41.08, -10.88) * mm});
            skLineSegment(sketch, "E969", {"start": v(-41.08, -10.88) * mm, "end": v(-41.85, -10.4) * mm});
            skLineSegment(sketch, "E970", {"start": v(-41.85, -10.4) * mm, "end": v(-42.6, -9.86) * mm});
            skLineSegment(sketch, "E971", {"start": v(-42.6, -9.86) * mm, "end": v(-43.3, -9.3) * mm});
            skLineSegment(sketch, "E972", {"start": v(-43.3, -9.3) * mm, "end": v(-44, -8.7) * mm});
            skLineSegment(sketch, "E973", {"start": v(-44, -8.7) * mm, "end": v(-44.65, -8.08) * mm});
            skLineSegment(sketch, "E974", {"start": v(-44.65, -8.08) * mm, "end": v(-45.28, -7.42) * mm});
            skLineSegment(sketch, "E975", {"start": v(-45.28, -7.42) * mm, "end": v(-45.87, -6.74) * mm});
            skLineSegment(sketch, "E976", {"start": v(-45.87, -6.74) * mm, "end": v(-46.43, -6.02) * mm});
            skLineSegment(sketch, "E977", {"start": v(-46.43, -6.02) * mm, "end": v(-46.96, -5.28) * mm});
            skLineSegment(sketch, "E978", {"start": v(-46.96, -5.28) * mm, "end": v(-47.45, -4.51) * mm});
            skLineSegment(sketch, "E979", {"start": v(-47.45, -4.51) * mm, "end": v(-47.91, -3.72) * mm});
            skLineSegment(sketch, "E980", {"start": v(-47.91, -3.72) * mm, "end": v(-48.33, -2.9) * mm});
            skLineSegment(sketch, "E981", {"start": v(-48.33, -2.9) * mm, "end": v(-48.7, -2.07) * mm});
            skLineSegment(sketch, "E982", {"start": v(-48.7, -2.07) * mm, "end": v(-49.05, -1.2) * mm});
            skLineSegment(sketch, "E983", {"start": v(-49.05, -1.2) * mm, "end": v(-49.34, -0.33) * mm});
            skLineSegment(sketch, "E984", {"start": v(-49.34, -0.33) * mm, "end": v(-49.6, 0.57) * mm});
            skLineSegment(sketch, "E985", {"start": v(-49.6, 0.57) * mm, "end": v(-49.81, 1.48) * mm});
            skLineSegment(sketch, "E986", {"start": v(-49.81, 1.48) * mm, "end": v(-49.98, 2.41) * mm});
            skLineSegment(sketch, "E987", {"start": v(-49.98, 2.41) * mm, "end": v(-50.1, 3.36) * mm});
            skLineSegment(sketch, "E988", {"start": v(-50.1, 3.36) * mm, "end": v(-50.17, 4.32) * mm});
            skLineSegment(sketch, "E989", {"start": v(-50.17, 4.32) * mm, "end": v(-50.2, 5.3) * mm});
            skLineSegment(sketch, "E990", {"start": v(-50.2, 5.3) * mm, "end": v(-50.17, 6.26) * mm});
            skLineSegment(sketch, "E991", {"start": v(-50.17, 6.26) * mm, "end": v(-50.1, 7.22) * mm});
            skLineSegment(sketch, "E992", {"start": v(-50.1, 7.22) * mm, "end": v(-49.98, 8.17) * mm});
            skLineSegment(sketch, "E993", {"start": v(-49.98, 8.17) * mm, "end": v(-49.81, 9.1) * mm});
            skLineSegment(sketch, "E994", {"start": v(-49.81, 9.1) * mm, "end": v(-49.6, 10.01) * mm});
            skLineSegment(sketch, "E995", {"start": v(-49.6, 10.01) * mm, "end": v(-49.34, 10.9) * mm});
            skLineSegment(sketch, "E996", {"start": v(-49.34, 10.9) * mm, "end": v(-49.05, 11.79) * mm});
            skLineSegment(sketch, "E997", {"start": v(-49.05, 11.79) * mm, "end": v(-48.7, 12.65) * mm});
            skLineSegment(sketch, "E998", {"start": v(-48.7, 12.65) * mm, "end": v(-48.33, 13.48) * mm});
            skLineSegment(sketch, "E999", {"start": v(-48.33, 13.48) * mm, "end": v(-47.91, 14.3) * mm});
            skLineSegment(sketch, "E1000", {"start": v(-47.91, 14.3) * mm, "end": v(-47.45, 15.1) * mm});
            skLineSegment(sketch, "E1001", {"start": v(-47.45, 15.1) * mm, "end": v(-46.96, 15.86) * mm});
            skLineSegment(sketch, "E1002", {"start": v(-46.96, 15.86) * mm, "end": v(-46.43, 16.6) * mm});
            skLineSegment(sketch, "E1003", {"start": v(-46.43, 16.6) * mm, "end": v(-45.87, 17.32) * mm});
            skLineSegment(sketch, "E1004", {"start": v(-45.87, 17.32) * mm, "end": v(-45.28, 18) * mm});
            skLineSegment(sketch, "E1005", {"start": v(-45.28, 18) * mm, "end": v(-44.65, 18.66) * mm});
            skLineSegment(sketch, "E1006", {"start": v(-44.65, 18.66) * mm, "end": v(-44, 19.29) * mm});
            skLineSegment(sketch, "E1007", {"start": v(-44, 19.29) * mm, "end": v(-43.3, 19.88) * mm});
            skLineSegment(sketch, "E1008", {"start": v(-43.3, 19.88) * mm, "end": v(-42.6, 20.44) * mm});
            skLineSegment(sketch, "E1009", {"start": v(-42.6, 20.44) * mm, "end": v(-41.85, 20.97) * mm});
            skLineSegment(sketch, "E1010", {"start": v(-41.85, 20.97) * mm, "end": v(-41.08, 21.46) * mm});
            skLineSegment(sketch, "E1011", {"start": v(-41.08, 21.46) * mm, "end": v(-40.29, 21.92) * mm});
            skLineSegment(sketch, "E1012", {"start": v(-40.29, 21.92) * mm, "end": v(-39.47, 22.34) * mm});
            skLineSegment(sketch, "E1013", {"start": v(-39.47, 22.34) * mm, "end": v(-38.64, 22.72) * mm});
            skLineSegment(sketch, "E1014", {"start": v(-38.64, 22.72) * mm, "end": v(-37.78, 23.06) * mm});
            skLineSegment(sketch, "E1015", {"start": v(-37.78, 23.06) * mm, "end": v(-36.9, 23.36) * mm});
            skLineSegment(sketch, "E1016", {"start": v(-36.9, 23.36) * mm, "end": v(-36, 23.61) * mm});
            skLineSegment(sketch, "E1017", {"start": v(-36, 23.61) * mm, "end": v(-35.09, 23.82) * mm});
            skLineSegment(sketch, "E1018", {"start": v(-35.09, 23.82) * mm, "end": v(-34.16, 23.99) * mm});
            skLineSegment(sketch, "E1019", {"start": v(-34.16, 23.99) * mm, "end": v(-33.21, 24.1) * mm});
            skLineSegment(sketch, "E1020", {"start": v(-33.21, 24.1) * mm, "end": v(-32.25, 24.18) * mm});
            skLineSegment(sketch, "E1021", {"start": v(-32.25, 24.18) * mm, "end": v(-31.28, 24.2) * mm});
            skLineSegment(sketch, "E1022", {"start": v(-31.28, 24.2) * mm, "end": v(-30.3, 24.18) * mm});
            skLineSegment(sketch, "E1023", {"start": v(-30.3, 24.18) * mm, "end": v(-29.35, 24.1) * mm});
            skLineSegment(sketch, "E1024", {"start": v(-29.35, 24.1) * mm, "end": v(-28.4, 23.99) * mm});
            skLineSegment(sketch, "E1025", {"start": v(-28.4, 23.99) * mm, "end": v(-27.47, 23.82) * mm});
            skLineSegment(sketch, "E1026", {"start": v(-27.47, 23.82) * mm, "end": v(-26.56, 23.61) * mm});
            skLineSegment(sketch, "E1027", {"start": v(-26.56, 23.61) * mm, "end": v(-25.66, 23.36) * mm});
            skLineSegment(sketch, "E1028", {"start": v(-25.66, 23.36) * mm, "end": v(-24.78, 23.06) * mm});
            skLineSegment(sketch, "E1029", {"start": v(-24.78, 23.06) * mm, "end": v(-23.92, 22.72) * mm});
            skLineSegment(sketch, "E1030", {"start": v(-23.92, 22.72) * mm, "end": v(-23.09, 22.34) * mm});
            skLineSegment(sketch, "E1031", {"start": v(-23.09, 22.34) * mm, "end": v(-22.27, 21.92) * mm});
            skLineSegment(sketch, "E1032", {"start": v(-22.27, 21.92) * mm, "end": v(-21.48, 21.46) * mm});
            skLineSegment(sketch, "E1033", {"start": v(-21.48, 21.46) * mm, "end": v(-20.7, 20.97) * mm});
            skLineSegment(sketch, "E1034", {"start": v(-20.7, 20.97) * mm, "end": v(-19.97, 20.44) * mm});
            skLineSegment(sketch, "E1035", {"start": v(-19.97, 20.44) * mm, "end": v(-19.25, 19.88) * mm});
            skLineSegment(sketch, "E1036", {"start": v(-19.25, 19.88) * mm, "end": v(-18.57, 19.29) * mm});
            skLineSegment(sketch, "E1037", {"start": v(-18.57, 19.29) * mm, "end": v(-17.9, 18.66) * mm});
            skLineSegment(sketch, "E1038", {"start": v(-17.9, 18.66) * mm, "end": v(-17.28, 18) * mm});
            skLineSegment(sketch, "E1039", {"start": v(-17.28, 18) * mm, "end": v(-16.69, 17.32) * mm});
            skLineSegment(sketch, "E1040", {"start": v(-16.69, 17.32) * mm, "end": v(-16.12, 16.6) * mm});
            skLineSegment(sketch, "E1041", {"start": v(-16.12, 16.6) * mm, "end": v(-15.6, 15.86) * mm});
            skLineSegment(sketch, "E1042", {"start": v(-15.6, 15.86) * mm, "end": v(-15.1, 15.1) * mm});
            skLineSegment(sketch, "E1043", {"start": v(-15.1, 15.1) * mm, "end": v(-14.65, 14.3) * mm});
            skLineSegment(sketch, "E1044", {"start": v(-14.65, 14.3) * mm, "end": v(-14.23, 13.48) * mm});
            skLineSegment(sketch, "E1045", {"start": v(-14.23, 13.48) * mm, "end": v(-13.85, 12.65) * mm});
            skLineSegment(sketch, "E1046", {"start": v(-13.85, 12.65) * mm, "end": v(-13.51, 11.79) * mm});
            skLineSegment(sketch, "E1047", {"start": v(-13.51, 11.79) * mm, "end": v(-13.21, 10.9) * mm});
            skLineSegment(sketch, "E1048", {"start": v(-13.21, 10.9) * mm, "end": v(-12.96, 10.01) * mm});
            skLineSegment(sketch, "E1049", {"start": v(-12.96, 10.01) * mm, "end": v(-12.75, 9.1) * mm});
            skLineSegment(sketch, "E1050", {"start": v(-12.75, 9.1) * mm, "end": v(-12.58, 8.17) * mm});
            skLineSegment(sketch, "E1051", {"start": v(-12.58, 8.17) * mm, "end": v(-12.46, 7.22) * mm});
            skLineSegment(sketch, "E1052", {"start": v(-12.46, 7.22) * mm, "end": v(-12.39, 6.26) * mm});
            skLineSegment(sketch, "E1053", {"start": v(-12.39, 6.26) * mm, "end": v(-12.36, 5.3) * mm});
            skLineSegment(sketch, "E1054", {"start": v(-12.36, 5.3) * mm, "end": v(-12.39, 4.32) * mm});
            skLineSegment(sketch, "E1055", {"start": v(51.98, 4.32) * mm, "end": v(51.91, 3.36) * mm});
            skLineSegment(sketch, "E1056", {"start": v(51.91, 3.36) * mm, "end": v(51.79, 2.41) * mm});
            skLineSegment(sketch, "E1057", {"start": v(51.79, 2.41) * mm, "end": v(51.62, 1.48) * mm});
            skLineSegment(sketch, "E1058", {"start": v(51.62, 1.48) * mm, "end": v(51.41, 0.57) * mm});
            skLineSegment(sketch, "E1059", {"start": v(51.41, 0.57) * mm, "end": v(51.16, -0.33) * mm});
            skLineSegment(sketch, "E1060", {"start": v(51.16, -0.33) * mm, "end": v(50.86, -1.2) * mm});
            skLineSegment(sketch, "E1061", {"start": v(50.86, -1.2) * mm, "end": v(50.52, -2.07) * mm});
            skLineSegment(sketch, "E1062", {"start": v(50.52, -2.07) * mm, "end": v(50.14, -2.9) * mm});
            skLineSegment(sketch, "E1063", {"start": v(50.14, -2.9) * mm, "end": v(49.72, -3.72) * mm});
            skLineSegment(sketch, "E1064", {"start": v(49.72, -3.72) * mm, "end": v(49.27, -4.51) * mm});
            skLineSegment(sketch, "E1065", {"start": v(49.27, -4.51) * mm, "end": v(48.77, -5.28) * mm});
            skLineSegment(sketch, "E1066", {"start": v(48.77, -5.28) * mm, "end": v(48.25, -6.02) * mm});
            skLineSegment(sketch, "E1067", {"start": v(48.25, -6.02) * mm, "end": v(47.68, -6.74) * mm});
            skLineSegment(sketch, "E1068", {"start": v(47.68, -6.74) * mm, "end": v(47.09, -7.42) * mm});
            skLineSegment(sketch, "E1069", {"start": v(47.09, -7.42) * mm, "end": v(46.46, -8.08) * mm});
            skLineSegment(sketch, "E1070", {"start": v(46.46, -8.08) * mm, "end": v(45.8, -8.7) * mm});
            skLineSegment(sketch, "E1071", {"start": v(45.8, -8.7) * mm, "end": v(45.12, -9.3) * mm});
            skLineSegment(sketch, "E1072", {"start": v(45.12, -9.3) * mm, "end": v(44.4, -9.86) * mm});
            skLineSegment(sketch, "E1073", {"start": v(44.4, -9.86) * mm, "end": v(43.66, -10.4) * mm});
            skLineSegment(sketch, "E1074", {"start": v(43.66, -10.4) * mm, "end": v(42.9, -10.88) * mm});
            skLineSegment(sketch, "E1075", {"start": v(42.9, -10.88) * mm, "end": v(42.1, -11.34) * mm});
            skLineSegment(sketch, "E1076", {"start": v(42.1, -11.34) * mm, "end": v(41.29, -11.76) * mm});
            skLineSegment(sketch, "E1077", {"start": v(41.29, -11.76) * mm, "end": v(40.45, -12.14) * mm});
            skLineSegment(sketch, "E1078", {"start": v(40.45, -12.14) * mm, "end": v(39.59, -12.48) * mm});
            skLineSegment(sketch, "E1079", {"start": v(39.59, -12.48) * mm, "end": v(38.71, -12.78) * mm});
            skLineSegment(sketch, "E1080", {"start": v(38.71, -12.78) * mm, "end": v(37.81, -13.03) * mm});
            skLineSegment(sketch, "E1081", {"start": v(37.81, -13.03) * mm, "end": v(36.9, -13.24) * mm});
            skLineSegment(sketch, "E1082", {"start": v(36.9, -13.24) * mm, "end": v(35.97, -13.4) * mm});
            skLineSegment(sketch, "E1083", {"start": v(35.97, -13.4) * mm, "end": v(35.02, -13.53) * mm});
            skLineSegment(sketch, "E1084", {"start": v(35.02, -13.53) * mm, "end": v(34.06, -13.6) * mm});
            skLineSegment(sketch, "E1085", {"start": v(34.06, -13.6) * mm, "end": v(33.1, -13.63) * mm});
            skLineSegment(sketch, "E1086", {"start": v(33.1, -13.63) * mm, "end": v(32.12, -13.6) * mm});
            skLineSegment(sketch, "E1087", {"start": v(32.12, -13.6) * mm, "end": v(31.16, -13.53) * mm});
            skLineSegment(sketch, "E1088", {"start": v(31.16, -13.53) * mm, "end": v(30.21, -13.4) * mm});
            skLineSegment(sketch, "E1089", {"start": v(30.21, -13.4) * mm, "end": v(29.28, -13.24) * mm});
            skLineSegment(sketch, "E1090", {"start": v(29.28, -13.24) * mm, "end": v(28.37, -13.03) * mm});
            skLineSegment(sketch, "E1091", {"start": v(28.37, -13.03) * mm, "end": v(27.47, -12.78) * mm});
            skLineSegment(sketch, "E1092", {"start": v(27.47, -12.78) * mm, "end": v(26.6, -12.48) * mm});
            skLineSegment(sketch, "E1093", {"start": v(26.6, -12.48) * mm, "end": v(25.73, -12.14) * mm});
            skLineSegment(sketch, "E1094", {"start": v(25.73, -12.14) * mm, "end": v(24.9, -11.76) * mm});
            skLineSegment(sketch, "E1095", {"start": v(24.9, -11.76) * mm, "end": v(24.08, -11.34) * mm});
            skLineSegment(sketch, "E1096", {"start": v(24.08, -11.34) * mm, "end": v(23.29, -10.88) * mm});
            skLineSegment(sketch, "E1097", {"start": v(23.29, -10.88) * mm, "end": v(22.52, -10.4) * mm});
            skLineSegment(sketch, "E1098", {"start": v(22.52, -10.4) * mm, "end": v(21.78, -9.86) * mm});
            skLineSegment(sketch, "E1099", {"start": v(21.78, -9.86) * mm, "end": v(21.07, -9.3) * mm});
            skLineSegment(sketch, "E1100", {"start": v(21.07, -9.3) * mm, "end": v(20.38, -8.7) * mm});
            skLineSegment(sketch, "E1101", {"start": v(20.38, -8.7) * mm, "end": v(19.72, -8.08) * mm});
            skLineSegment(sketch, "E1102", {"start": v(19.72, -8.08) * mm, "end": v(19.1, -7.42) * mm});
            skLineSegment(sketch, "E1103", {"start": v(19.1, -7.42) * mm, "end": v(18.5, -6.74) * mm});
            skLineSegment(sketch, "E1104", {"start": v(18.5, -6.74) * mm, "end": v(17.94, -6.02) * mm});
            skLineSegment(sketch, "E1105", {"start": v(17.94, -6.02) * mm, "end": v(17.4, -5.28) * mm});
            skLineSegment(sketch, "E1106", {"start": v(17.4, -5.28) * mm, "end": v(16.92, -4.51) * mm});
            skLineSegment(sketch, "E1107", {"start": v(16.92, -4.51) * mm, "end": v(16.46, -3.72) * mm});
            skLineSegment(sketch, "E1108", {"start": v(16.46, -3.72) * mm, "end": v(16.04, -2.9) * mm});
            skLineSegment(sketch, "E1109", {"start": v(16.04, -2.9) * mm, "end": v(15.66, -2.07) * mm});
            skLineSegment(sketch, "E1110", {"start": v(15.66, -2.07) * mm, "end": v(15.32, -1.2) * mm});
            skLineSegment(sketch, "E1111", {"start": v(15.32, -1.2) * mm, "end": v(15.03, -0.33) * mm});
            skLineSegment(sketch, "E1112", {"start": v(15.03, -0.33) * mm, "end": v(14.77, 0.57) * mm});
            skLineSegment(sketch, "E1113", {"start": v(14.77, 0.57) * mm, "end": v(14.56, 1.48) * mm});
            skLineSegment(sketch, "E1114", {"start": v(14.56, 1.48) * mm, "end": v(14.4, 2.41) * mm});
            skLineSegment(sketch, "E1115", {"start": v(14.4, 2.41) * mm, "end": v(14.27, 3.36) * mm});
            skLineSegment(sketch, "E1116", {"start": v(14.27, 3.36) * mm, "end": v(14.2, 4.32) * mm});
            skLineSegment(sketch, "E1117", {"start": v(14.2, 4.32) * mm, "end": v(14.17, 5.3) * mm});
            skLineSegment(sketch, "E1118", {"start": v(14.17, 5.3) * mm, "end": v(14.2, 6.26) * mm});
            skLineSegment(sketch, "E1119", {"start": v(14.2, 6.26) * mm, "end": v(14.27, 7.22) * mm});
            skLineSegment(sketch, "E1120", {"start": v(14.27, 7.22) * mm, "end": v(14.4, 8.17) * mm});
            skLineSegment(sketch, "E1121", {"start": v(14.4, 8.17) * mm, "end": v(14.56, 9.1) * mm});
            skLineSegment(sketch, "E1122", {"start": v(14.56, 9.1) * mm, "end": v(14.77, 10.01) * mm});
            skLineSegment(sketch, "E1123", {"start": v(14.77, 10.01) * mm, "end": v(15.03, 10.9) * mm});
            skLineSegment(sketch, "E1124", {"start": v(15.03, 10.9) * mm, "end": v(15.32, 11.79) * mm});
            skLineSegment(sketch, "E1125", {"start": v(15.32, 11.79) * mm, "end": v(15.66, 12.65) * mm});
            skLineSegment(sketch, "E1126", {"start": v(15.66, 12.65) * mm, "end": v(16.04, 13.48) * mm});
            skLineSegment(sketch, "E1127", {"start": v(16.04, 13.48) * mm, "end": v(16.46, 14.3) * mm});
            skLineSegment(sketch, "E1128", {"start": v(16.46, 14.3) * mm, "end": v(16.92, 15.1) * mm});
            skLineSegment(sketch, "E1129", {"start": v(16.92, 15.1) * mm, "end": v(17.4, 15.86) * mm});
            skLineSegment(sketch, "E1130", {"start": v(17.4, 15.86) * mm, "end": v(17.94, 16.6) * mm});
            skLineSegment(sketch, "E1131", {"start": v(17.94, 16.6) * mm, "end": v(18.5, 17.32) * mm});
            skLineSegment(sketch, "E1132", {"start": v(18.5, 17.32) * mm, "end": v(19.1, 18) * mm});
            skLineSegment(sketch, "E1133", {"start": v(19.1, 18) * mm, "end": v(19.72, 18.66) * mm});
            skLineSegment(sketch, "E1134", {"start": v(19.72, 18.66) * mm, "end": v(20.38, 19.29) * mm});
            skLineSegment(sketch, "E1135", {"start": v(20.38, 19.29) * mm, "end": v(21.07, 19.88) * mm});
            skLineSegment(sketch, "E1136", {"start": v(21.07, 19.88) * mm, "end": v(21.78, 20.44) * mm});
            skLineSegment(sketch, "E1137", {"start": v(21.78, 20.44) * mm, "end": v(22.52, 20.97) * mm});
            skLineSegment(sketch, "E1138", {"start": v(22.52, 20.97) * mm, "end": v(23.29, 21.46) * mm});
            skLineSegment(sketch, "E1139", {"start": v(23.29, 21.46) * mm, "end": v(24.08, 21.92) * mm});
            skLineSegment(sketch, "E1140", {"start": v(24.08, 21.92) * mm, "end": v(24.9, 22.34) * mm});
            skLineSegment(sketch, "E1141", {"start": v(24.9, 22.34) * mm, "end": v(25.73, 22.72) * mm});
            skLineSegment(sketch, "E1142", {"start": v(25.73, 22.72) * mm, "end": v(26.6, 23.06) * mm});
            skLineSegment(sketch, "E1143", {"start": v(26.6, 23.06) * mm, "end": v(27.47, 23.36) * mm});
            skLineSegment(sketch, "E1144", {"start": v(27.47, 23.36) * mm, "end": v(28.37, 23.61) * mm});
            skLineSegment(sketch, "E1145", {"start": v(28.37, 23.61) * mm, "end": v(29.28, 23.82) * mm});
            skLineSegment(sketch, "E1146", {"start": v(29.28, 23.82) * mm, "end": v(30.21, 23.99) * mm});
            skLineSegment(sketch, "E1147", {"start": v(30.21, 23.99) * mm, "end": v(31.16, 24.1) * mm});
            skLineSegment(sketch, "E1148", {"start": v(31.16, 24.1) * mm, "end": v(32.12, 24.18) * mm});
            skLineSegment(sketch, "E1149", {"start": v(32.12, 24.18) * mm, "end": v(33.1, 24.2) * mm});
            skLineSegment(sketch, "E1150", {"start": v(33.1, 24.2) * mm, "end": v(34.06, 24.18) * mm});
            skLineSegment(sketch, "E1151", {"start": v(34.06, 24.18) * mm, "end": v(35.02, 24.1) * mm});
            skLineSegment(sketch, "E1152", {"start": v(35.02, 24.1) * mm, "end": v(35.97, 23.99) * mm});
            skLineSegment(sketch, "E1153", {"start": v(35.97, 23.99) * mm, "end": v(36.9, 23.82) * mm});
            skLineSegment(sketch, "E1154", {"start": v(36.9, 23.82) * mm, "end": v(37.81, 23.61) * mm});
            skLineSegment(sketch, "E1155", {"start": v(37.81, 23.61) * mm, "end": v(38.71, 23.36) * mm});
            skLineSegment(sketch, "E1156", {"start": v(38.71, 23.36) * mm, "end": v(39.59, 23.06) * mm});
            skLineSegment(sketch, "E1157", {"start": v(39.59, 23.06) * mm, "end": v(40.45, 22.72) * mm});
            skLineSegment(sketch, "E1158", {"start": v(40.45, 22.72) * mm, "end": v(41.29, 22.34) * mm});
            skLineSegment(sketch, "E1159", {"start": v(41.29, 22.34) * mm, "end": v(42.1, 21.92) * mm});
            skLineSegment(sketch, "E1160", {"start": v(42.1, 21.92) * mm, "end": v(42.9, 21.46) * mm});
            skLineSegment(sketch, "E1161", {"start": v(42.9, 21.46) * mm, "end": v(43.66, 20.97) * mm});
            skLineSegment(sketch, "E1162", {"start": v(43.66, 20.97) * mm, "end": v(44.4, 20.44) * mm});
            skLineSegment(sketch, "E1163", {"start": v(44.4, 20.44) * mm, "end": v(45.12, 19.88) * mm});
            skLineSegment(sketch, "E1164", {"start": v(45.12, 19.88) * mm, "end": v(45.8, 19.29) * mm});
            skLineSegment(sketch, "E1165", {"start": v(45.8, 19.29) * mm, "end": v(46.46, 18.66) * mm});
            skLineSegment(sketch, "E1166", {"start": v(46.46, 18.66) * mm, "end": v(47.09, 18) * mm});
            skLineSegment(sketch, "E1167", {"start": v(47.09, 18) * mm, "end": v(47.68, 17.32) * mm});
            skLineSegment(sketch, "E1168", {"start": v(47.68, 17.32) * mm, "end": v(48.25, 16.6) * mm});
            skLineSegment(sketch, "E1169", {"start": v(48.25, 16.6) * mm, "end": v(48.77, 15.86) * mm});
            skLineSegment(sketch, "E1170", {"start": v(48.77, 15.86) * mm, "end": v(49.27, 15.1) * mm});
            skLineSegment(sketch, "E1171", {"start": v(49.27, 15.1) * mm, "end": v(49.72, 14.3) * mm});
            skLineSegment(sketch, "E1172", {"start": v(49.72, 14.3) * mm, "end": v(50.14, 13.48) * mm});
            skLineSegment(sketch, "E1173", {"start": v(50.14, 13.48) * mm, "end": v(50.52, 12.65) * mm});
            skLineSegment(sketch, "E1174", {"start": v(50.52, 12.65) * mm, "end": v(50.86, 11.79) * mm});
            skLineSegment(sketch, "E1175", {"start": v(50.86, 11.79) * mm, "end": v(51.16, 10.9) * mm});
            skLineSegment(sketch, "E1176", {"start": v(51.16, 10.9) * mm, "end": v(51.41, 10.01) * mm});
            skLineSegment(sketch, "E1177", {"start": v(51.41, 10.01) * mm, "end": v(51.62, 9.1) * mm});
            skLineSegment(sketch, "E1178", {"start": v(51.62, 9.1) * mm, "end": v(51.79, 8.17) * mm});
            skLineSegment(sketch, "E1179", {"start": v(51.79, 8.17) * mm, "end": v(51.91, 7.22) * mm});
            skLineSegment(sketch, "E1180", {"start": v(51.91, 7.22) * mm, "end": v(51.98, 6.26) * mm});
            skLineSegment(sketch, "E1181", {"start": v(51.98, 6.26) * mm, "end": v(52, 5.3) * mm});
            skLineSegment(sketch, "E1182", {"start": v(52, 5.3) * mm, "end": v(51.98, 4.32) * mm});
            skSolve(sketch);
        }
        {
            var Q0;
            Q0 = qSketchRegion(id + "F0", true);
            extrude(context, id + "F1", {"entities" : qUnion([Q0]), "depth" : 6 * mm});
        }
    });
